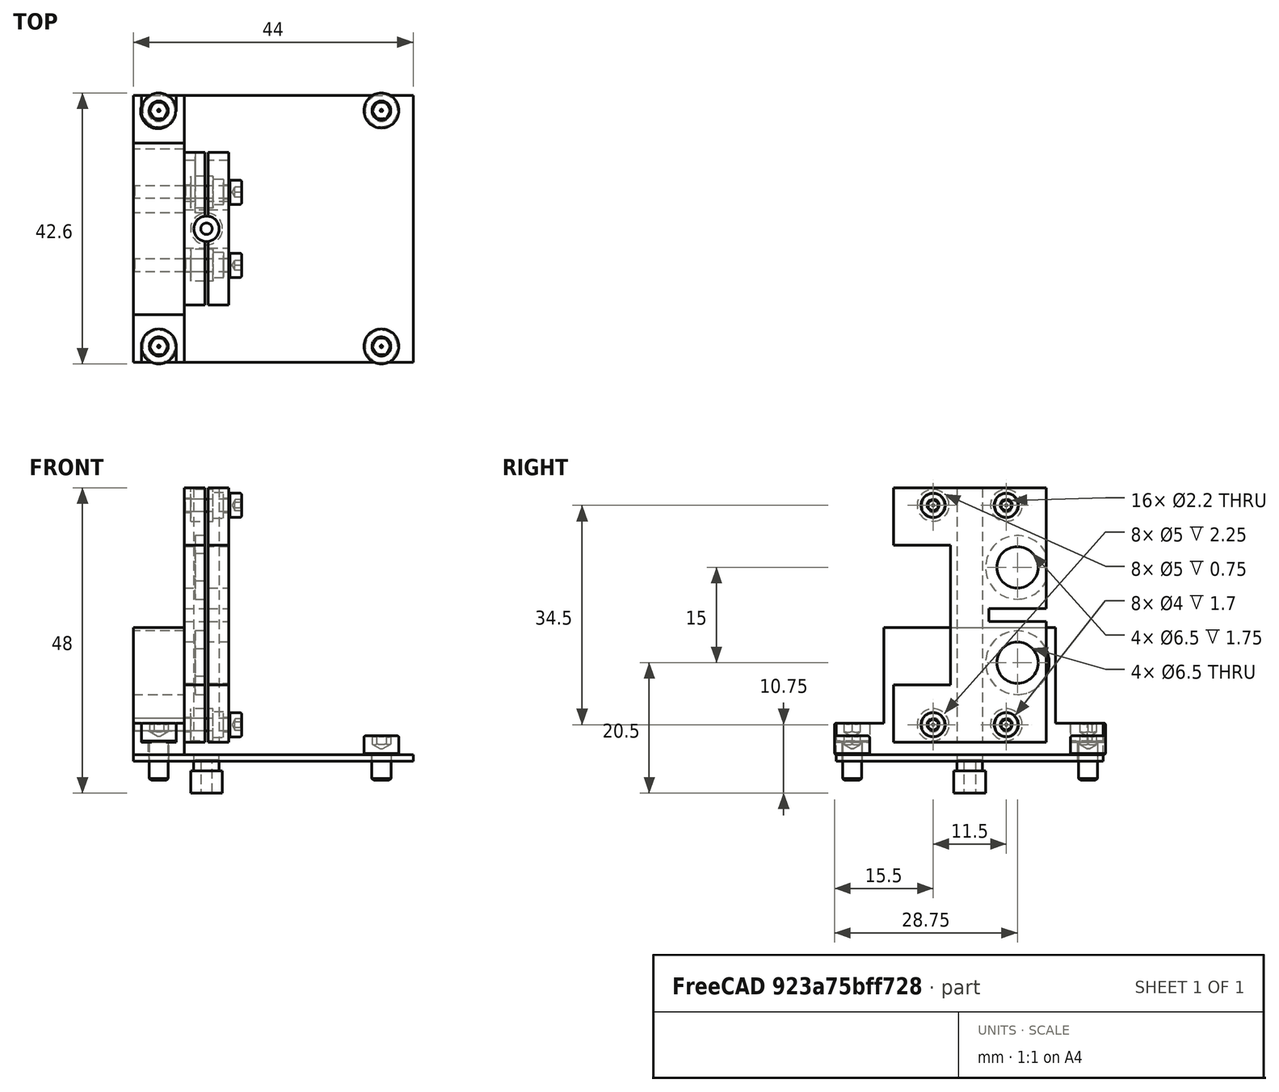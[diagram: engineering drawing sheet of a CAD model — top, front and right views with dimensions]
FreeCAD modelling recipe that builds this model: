
FCSTD DOCUMENT  (FreeCAD 0.22R0.21.2)
Label: Quak_XL30_Modulator2
License: All rights reserved
LicenseURL: http://en.wikipedia.org/wiki/All_rights_reserved
objects: TechDraw::DrawViewDimension×105, Part::Cylinder×38, Part::MultiFuse×22, App::Link×17, TechDraw::DrawProjGroupItem×12, Part::Box×11, Part::Cut×11, Part::FeaturePython×8, TechDraw::DrawSVGTemplate×8, TechDraw::DrawPage×8, Part::Feature×8, TechDraw::DrawProjGroup×4, TechDraw::DrawViewAnnotation×4, TechDraw::DrawViewPart×4, TechDraw::DrawViewSection×4, Spreadsheet::Sheet×1, Part::Compound×1
note: 264 computed .brp shape members not serialized (recipe doc carries the construction recipe); baked Part::Feature solids carry a one-line shape summary decoded from their .brp
EXTERNAL_REF file=XL30ColumnAttachmentRing_PCBKicker01.FCStd obj=Cut007
EXTERNAL_REF file=../../Spacers/Macor/4mmOD_M2_5.5mm.FCStd obj=Cut

FEATURE [Spreadsheet::Sheet] Spreadsheet  label="ModulatorParameters"
  cells = A2='Beamhole diameter; B2(beamhole_diameter)=3; G2='epsilon_r; H2(e_r)=3.5; I2='Kapton: 3.5, Vacuum 0; K2='Vacuum 'Permitivity (e0); L2='8.854187e-12; A3='Insulation spacing; B3(insulation_spacing)=0.5; G3='mu_r; H3(mu_r)=1; K3='Vacuum 'Permeability (mu0); L3='1.257e-06; A4='Maximum hole diameter; B4(max_beamhole_diameter)=6; G4='Intrinsic impedance; H4(eta_intrinsic_impedance)==sqrt(mu_r * 1.257e-06 / (e_r * 8.854187e-12)); A5='Holder minimum length; B5(holderminlength)=20; G5='Kicker imepdance; H5='=eta_intrinsic_impedance * insulation_spacing / (kicker_inner_width * kicker_plate_length); A6='Kicker length; B6(kicker_length)=40
FEATURE [App::Link] Link  label="Stackmountring02"
  LinkedObject = -> <external XL30ColumnAttachmentRing_PCBKicker01.FCStd>#Cut007
FEATURE [Part::Box] Box  label="Cube"
  AttacherType = Attacher::AttachEngine3D
  Height = 5
  Length = 8
  Placement = pos=(-11.5,-21,5) rot=(0,0,1;0rad)
  Width = 42
FEATURE [Part::FeaturePython] Screw  label="M3x6-Screw"  # Fasteners workbench fastener (typed FeaturePython)
  Placement = pos=(-7.5,18.6,8) rot=(1,0,0;0rad)
  diameter = 4
  invert = false
  leftHanded = false
  length = 10
  lengthCustom = 6
  matchOuter = false
  offset = 0
  thread = false
  type = 48
FEATURE [Part::Cylinder] Cylinder
  Angle = 360
  AttacherType = Attacher::AttachEngine3D
  FirstAngle = 0
  Height = 5
  Radius = 1.6
  SecondAngle = 0
FEATURE [Part::Cylinder] Cylinder001
  Angle = 360
  AttacherType = Attacher::AttachEngine3D
  FirstAngle = 0
  Height = 3
  Placement = pos=(0,0,2) rot=(0,0,1;0rad)
  Radius = 2.75
  SecondAngle = 0
FEATURE [Part::MultiFuse] Fusion
  Placement = pos=(-7.6,18.5,5) rot=(0,0,1;0rad)
  Shapes = -> [Cylinder001,Cylinder]
FEATURE [Part::Cylinder] Cylinder002
  Angle = 360
  AttacherType = Attacher::AttachEngine3D
  FirstAngle = 0
  Height = 5
  Radius = 1.6
  SecondAngle = 0
FEATURE [Part::Cylinder] Cylinder003
  Angle = 360
  AttacherType = Attacher::AttachEngine3D
  FirstAngle = 0
  Height = 3
  Placement = pos=(0,0,2) rot=(0,0,1;0rad)
  Radius = 2.75
  SecondAngle = 0
FEATURE [Part::MultiFuse] Fusion001
  Placement = pos=(-7.5,-18.5,5) rot=(0,0,1;0rad)
  Shapes = -> [Cylinder003,Cylinder002]
FEATURE [Part::FeaturePython] Screw001  label="M3x6-Screw001"  # Fasteners workbench fastener (typed FeaturePython)
  Placement = pos=(-7.5,-18.5,8) rot=(1,0,0;0rad)
  diameter = 4
  invert = false
  leftHanded = false
  length = 10
  lengthCustom = 6
  matchOuter = false
  offset = 0
  thread = false
  type = 48
FEATURE [Part::Box] Box001  label="Cube001"
  AttacherType = Attacher::AttachEngine3D
  Height = 3
  Length = 5.5
  Placement = pos=(-10.25,18.5,7) rot=(0,0,1;0rad)
  Width = 5.5
FEATURE [Part::Box] Box002  label="Cube002"
  AttacherType = Attacher::AttachEngine3D
  Height = 3
  Length = 5.5
  Placement = pos=(-10.25,-24,7) rot=(0,0,1;0rad)
  Width = 5.5
FEATURE [Part::MultiFuse] Fusion002
  Shapes = -> [Fusion,Box001]
FEATURE [Part::MultiFuse] Fusion003
  Shapes = -> [Fusion001,Box002]
FEATURE [Part::MultiFuse] Fusion004
  Shapes = -> [Fusion002,Fusion003]
FEATURE [Part::Cut] Cut
  Base = -> Box
  Tool = -> Fusion004
FEATURE [Part::Box] Box003  label="Cube003"
  AttacherType = Attacher::AttachEngine3D
  Height = 20
  Length = 8
  Placement = pos=(-11.5,-13.5,5) rot=(0,0,1;0rad)
  Width = 27
  expr: .Placement.Base.y = -(2 * 5.5 + <<ModulatorParameters>>.max_beamhole_diameter + 10) / 2
  expr: Height = <<ModulatorParameters>>.holderminlength
  expr: Width = 2 * 5.5 + <<ModulatorParameters>>.max_beamhole_diameter + 10
FEATURE [Part::MultiFuse] Fusion005
  Shapes = -> [Cut,Box003]
FEATURE [Part::Box] Box004  label="Cube004"
  AttacherType = Attacher::AttachEngine3D
  Height = 40
  Length = 3.25
  Placement = pos=(-3.5,-12,0) rot=(0,0,1;0rad)
  Width = 24
  expr: .Placement.Base.y = -(2 * 9 + <<ModulatorParameters>>.max_beamhole_diameter) / 2
  expr: Height = <<ModulatorParameters>>.kicker_length
  expr: Length = 3.5 - <<ModulatorParameters>>.insulation_spacing / 2
  expr: Width = 2 * 9 + <<ModulatorParameters>>.max_beamhole_diameter
FEATURE [Part::Cylinder] Cylinder004  label="Beamhole"
  Angle = 360
  AttacherType = Attacher::AttachEngine3D
  FirstAngle = 0
  Height = 40
  Radius = 2
  SecondAngle = 0
  expr: Height = <<ModulatorParameters>>.kicker_length
FEATURE [Part::Cut] Cut001
  Base = -> Box004
  Placement = pos=(0,0,7) rot=(0,0,1;0rad)
  Tool = -> Cylinder004
FEATURE [App::Link] Link001  label="Markor4mmOD_M2"
  LinkPlacement = pos=(-2.5,-5.75,9.75) rot=(0,1,0;1.5708rad)
  LinkedObject = -> <external ../../Spacers/Macor/4mmOD_M2_5.5mm.FCStd>#Cut
  Placement = pos=(-2.5,-5.75,9.75) rot=(0,1,0;1.5708rad)
  expr: .Placement.Base.y = -<<ModulatorParameters>>.max_beamhole_diameter / 2 - 5.5 / 2
FEATURE [Part::Cylinder] Cylinder006
  Angle = 360
  AttacherType = Attacher::AttachEngine3D
  FirstAngle = 0
  Height = 10
  Placement = pos=(-3.5,-5.75,9.75) rot=(0,1,0;1.5708rad)
  Radius = 1.1
  SecondAngle = 0
  expr: .Placement.Base.y = -<<ModulatorParameters>>.max_beamhole_diameter / 2 - 5.5 / 2
FEATURE [Part::Cylinder] Cylinder007
  Angle = 360
  AttacherType = Attacher::AttachEngine3D
  FirstAngle = 0
  Height = 10
  Placement = pos=(-3.5,5.75,9.75) rot=(0,1,0;1.5708rad)
  Radius = 1.1
  SecondAngle = 0
  expr: .Placement.Base.y = <<ModulatorParameters>>.max_beamhole_diameter / 2 + 5.5 / 2
FEATURE [App::Link] Link002  label="Markor4mmOD_M003"
  LinkPlacement = pos=(-2.5,5.75,9.75) rot=(0,1,0;1.5708rad)
  LinkedObject = -> <external ../../Spacers/Macor/4mmOD_M2_5.5mm.FCStd>#Cut
  Placement = pos=(-2.5,5.75,9.75) rot=(0,1,0;1.5708rad)
  expr: .Placement.Base.y = <<ModulatorParameters>>.max_beamhole_diameter / 2 + 5.5 / 2
FEATURE [Part::MultiFuse] Fusion006
  Shapes = -> [Link001,Cylinder006,Cylinder007,Link002]
FEATURE [Part::Cylinder] Cylinder008
  Angle = 360
  AttacherType = Attacher::AttachEngine3D
  FirstAngle = 0
  Height = 10
  Placement = pos=(-3.5,-5.75,44.25) rot=(0,1,0;1.5708rad)
  Radius = 1.1
  SecondAngle = 0
  expr: .Placement.Base.y = -<<ModulatorParameters>>.max_beamhole_diameter / 2 - 5.5 / 2
  expr: .Placement.Base.z = 7 + <<ModulatorParameters>>.kicker_length - 5.5 / 2
FEATURE [Part::Cylinder] Cylinder009
  Angle = 360
  AttacherType = Attacher::AttachEngine3D
  FirstAngle = 0
  Height = 10
  Placement = pos=(-3.5,5.75,44.25) rot=(0,1,0;1.5708rad)
  Radius = 1.1
  SecondAngle = 0
  expr: .Placement.Base.y = <<ModulatorParameters>>.max_beamhole_diameter / 2 + 5.5 / 2
  expr: .Placement.Base.z = 7 + <<ModulatorParameters>>.kicker_length - 5.5 / 2
FEATURE [App::Link] Link003  label="Markor4mmOD_M004"
  LinkPlacement = pos=(-2.5,-5.75,44.25) rot=(0,1,0;1.5708rad)
  LinkedObject = -> <external ../../Spacers/Macor/4mmOD_M2_5.5mm.FCStd>#Cut
  Placement = pos=(-2.5,-5.75,44.25) rot=(0,1,0;1.5708rad)
  expr: .Placement.Base.y = -1 * (<<ModulatorParameters>>.max_beamhole_diameter / 2 + 5.5 / 2)
  expr: .Placement.Base.z = 7 + <<ModulatorParameters>>.kicker_length - 5.5 / 2
FEATURE [App::Link] Link004  label="Markor4mmOD_M005"
  LinkPlacement = pos=(-2.5,5.75,44.25) rot=(0,1,0;1.5708rad)
  LinkedObject = -> <external ../../Spacers/Macor/4mmOD_M2_5.5mm.FCStd>#Cut
  Placement = pos=(-2.5,5.75,44.25) rot=(0,1,0;1.5708rad)
  expr: .Placement.Base.y = <<ModulatorParameters>>.max_beamhole_diameter / 2 + 5.5 / 2
  expr: .Placement.Base.z = 7 + <<ModulatorParameters>>.kicker_length - 5.5 / 2
FEATURE [Part::MultiFuse] Fusion007
  Shapes = -> [Cylinder008,Cylinder009,Link003,Link004]
FEATURE [Part::Box] Box006  label="Cube006"
  AttacherType = Attacher::AttachEngine3D
  Height = 2
  Length = 3.25
  Placement = pos=(-3.5,3,26) rot=(0,0,1;0rad)
  Width = 9
  expr: .Placement.Base.y = <<ModulatorParameters>>.max_beamhole_diameter / 2
  expr: .Placement.Base.z = 7 + 9 + 10
  expr: Height = <<ModulatorParameters>>.kicker_length - 2 * 9 - 20
  expr: Length = 3.5 - <<ModulatorParameters>>.insulation_spacing / 2
FEATURE [Part::Box] Box007  label="Cube007"
  AttacherType = Attacher::AttachEngine3D
  Height = 22
  Length = 3.25
  Placement = pos=(-3.5,-12,16) rot=(0,0,1;0rad)
  Width = 9
  expr: .Placement.Base.y = -<<ModulatorParameters>>.max_beamhole_diameter / 2 - 9
  expr: .Placement.Base.z = 7 + 9
  expr: Height = <<ModulatorParameters>>.kicker_length - 2 * 9
  expr: Length = 3.5 - <<ModulatorParameters>>.insulation_spacing / 2
FEATURE [Part::Cylinder] Cylinder010
  Angle = 360
  AttacherType = Attacher::AttachEngine3D
  FirstAngle = 0
  Height = 10
  Placement = pos=(-3.5,7.5,34.5) rot=(0,1,0;1.5708rad)
  Radius = 3.25
  SecondAngle = 0
  expr: .Placement.Base.y = <<ModulatorParameters>>.max_beamhole_diameter / 2 + 9 / 2
  expr: .Placement.Base.z = 7 + <<ModulatorParameters>>.kicker_length - 9 - 7 / 2
FEATURE [Part::Cylinder] Cylinder011
  Angle = 360
  AttacherType = Attacher::AttachEngine3D
  FirstAngle = 0
  Height = 10
  Placement = pos=(-3.5,7.5,19.5) rot=(0,1,0;1.5708rad)
  Radius = 3.25
  SecondAngle = 0
  expr: .Placement.Base.y = <<ModulatorParameters>>.max_beamhole_diameter / 2 + 9 / 2
  expr: .Placement.Base.z = 7 + 9 + 7 / 2
FEATURE [Part::Cylinder] Cylinder012
  Angle = 360
  AttacherType = Attacher::AttachEngine3D
  FirstAngle = 0
  Height = 10
  Placement = pos=(-12.5,7.5,19.5) rot=(0,1,0;1.5708rad)
  Radius = 5
  SecondAngle = 0
  expr: .Placement.Base.y = <<ModulatorParameters>>.max_beamhole_diameter / 2 + 9 / 2
  expr: .Placement.Base.z = 7 + 9 + 7 / 2
FEATURE [Part::MultiFuse] Fusion008
  Placement = pos=(3.75,0,0) rot=(0,0,1;0rad)
  Shapes = -> [Cylinder011,Cylinder010,Box007,Box006]
FEATURE [Part::Cut] Cut002
  Base = -> Fusion005
  Tool = -> Cylinder012
FEATURE [Part::Box] Box008  label="Cube008"
  AttacherType = Attacher::AttachEngine3D
  Height = 40
  Length = 3.25
  Placement = pos=(-3.5,-12,0) rot=(0,0,1;0rad)
  Width = 24
  expr: .Placement.Base.y = -(2 * 9 + <<ModulatorParameters>>.max_beamhole_diameter) / 2
  expr: Height = <<ModulatorParameters>>.kicker_length
  expr: Length = 3.5 - <<ModulatorParameters>>.insulation_spacing / 2
  expr: Width = 2 * 9 + <<ModulatorParameters>>.max_beamhole_diameter
FEATURE [Part::Cylinder] Cylinder013  label="Beamhole001"
  Angle = 360
  AttacherType = Attacher::AttachEngine3D
  FirstAngle = 0
  Height = 40
  Radius = 2
  SecondAngle = 0
  expr: Height = <<ModulatorParameters>>.kicker_length
FEATURE [Part::Cut] Cut003
  Base = -> Box008
  Placement = pos=(0,0,7) rot=(0,0,1;3.14159rad)
  Tool = -> Cylinder013
FEATURE [Part::Box] Box009  label="Cube009"
  AttacherType = Attacher::AttachEngine3D
  Height = 2
  Length = 3.25
  Placement = pos=(-3.5,3,26) rot=(0,0,1;0rad)
  Width = 9
  expr: .Placement.Base.y = <<ModulatorParameters>>.max_beamhole_diameter / 2
  expr: .Placement.Base.z = 7 + 9 + 10
  expr: Height = <<ModulatorParameters>>.kicker_length - 2 * 9 - 20
  expr: Length = 3.5 - <<ModulatorParameters>>.insulation_spacing / 2
FEATURE [Part::Box] Box010  label="Cube010"
  AttacherType = Attacher::AttachEngine3D
  Height = 22
  Length = 3.25
  Placement = pos=(-3.5,-12,16) rot=(0,0,1;0rad)
  Width = 9
  expr: .Placement.Base.y = -<<ModulatorParameters>>.max_beamhole_diameter / 2 - 9
  expr: .Placement.Base.z = 7 + 9
  expr: Height = <<ModulatorParameters>>.kicker_length - 2 * 9
  expr: Length = 3.5 - <<ModulatorParameters>>.insulation_spacing / 2
FEATURE [Part::Cylinder] Cylinder014
  Angle = 360
  AttacherType = Attacher::AttachEngine3D
  FirstAngle = 0
  Height = 10
  Placement = pos=(-3.5,-5.75,9.75) rot=(0,1,0;1.5708rad)
  Radius = 1.1
  SecondAngle = 0
  expr: .Placement.Base.y = -<<ModulatorParameters>>.max_beamhole_diameter / 2 - 5.5 / 2
FEATURE [Part::Cylinder] Cylinder015
  Angle = 360
  AttacherType = Attacher::AttachEngine3D
  FirstAngle = 0
  Height = 10
  Placement = pos=(-3.5,5.75,9.75) rot=(0,1,0;1.5708rad)
  Radius = 1.1
  SecondAngle = 0
  expr: .Placement.Base.y = <<ModulatorParameters>>.max_beamhole_diameter / 2 + 5.5 / 2
FEATURE [Part::Cylinder] Cylinder016
  Angle = 360
  AttacherType = Attacher::AttachEngine3D
  FirstAngle = 0
  Height = 10
  Placement = pos=(-3.5,-5.75,44.25) rot=(0,1,0;1.5708rad)
  Radius = 1.1
  SecondAngle = 0
  expr: .Placement.Base.y = -<<ModulatorParameters>>.max_beamhole_diameter / 2 - 5.5 / 2
  expr: .Placement.Base.z = 7 + <<ModulatorParameters>>.kicker_length - 5.5 / 2
FEATURE [Part::Cylinder] Cylinder017
  Angle = 360
  AttacherType = Attacher::AttachEngine3D
  FirstAngle = 0
  Height = 10
  Placement = pos=(-3.5,5.75,44.25) rot=(0,1,0;1.5708rad)
  Radius = 1.1
  SecondAngle = 0
  expr: .Placement.Base.y = <<ModulatorParameters>>.max_beamhole_diameter / 2 + 5.5 / 2
  expr: .Placement.Base.z = 7 + <<ModulatorParameters>>.kicker_length - 5.5 / 2
FEATURE [Part::Cylinder] Cylinder018
  Angle = 360
  AttacherType = Attacher::AttachEngine3D
  FirstAngle = 0
  Height = 10
  Placement = pos=(-3.5,7.5,34.5) rot=(0,1,0;1.5708rad)
  Radius = 3.25
  SecondAngle = 0
  expr: .Placement.Base.y = <<ModulatorParameters>>.max_beamhole_diameter / 2 + 9 / 2
  expr: .Placement.Base.z = 7 + <<ModulatorParameters>>.kicker_length - 9 - 7 / 2
FEATURE [Part::Cylinder] Cylinder019
  Angle = 360
  AttacherType = Attacher::AttachEngine3D
  FirstAngle = 0
  Height = 10
  Placement = pos=(-3.5,7.5,19.5) rot=(0,1,0;1.5708rad)
  Radius = 3.25
  SecondAngle = 0
  expr: .Placement.Base.y = <<ModulatorParameters>>.max_beamhole_diameter / 2 + 9 / 2
  expr: .Placement.Base.z = 7 + 9 + 7 / 2
FEATURE [App::Link] Link005  label="Markor4mmOD_M006"
  LinkPlacement = pos=(-2.5,-5.75,9.75) rot=(0,1,0;1.5708rad)
  LinkedObject = -> Cut004
  Placement = pos=(-2.5,-5.75,9.75) rot=(0,1,0;1.5708rad)
  expr: .Placement.Base.y = -<<ModulatorParameters>>.max_beamhole_diameter / 2 - 5.5 / 2
FEATURE [App::Link] Link006  label="Markor4mmOD_M007"
  LinkPlacement = pos=(-2.5,5.75,9.75) rot=(0,1,0;1.5708rad)
  LinkedObject = -> Cut004
  Placement = pos=(-2.5,5.75,9.75) rot=(0,1,0;1.5708rad)
  expr: .Placement.Base.y = <<ModulatorParameters>>.max_beamhole_diameter / 2 + 5.5 / 2
FEATURE [Part::MultiFuse] Fusion009
  Shapes = -> [Link005,Cylinder014,Cylinder015,Link006]
FEATURE [App::Link] Link007  label="Markor4mmOD_M008"
  LinkPlacement = pos=(-2.5,-5.75,44.25) rot=(0,1,0;1.5708rad)
  LinkedObject = -> Cut004
  Placement = pos=(-2.5,-5.75,44.25) rot=(0,1,0;1.5708rad)
  expr: .Placement.Base.y = -1 * (<<ModulatorParameters>>.max_beamhole_diameter / 2 + 5.5 / 2)
  expr: .Placement.Base.z = 7 + <<ModulatorParameters>>.kicker_length - 5.5 / 2
FEATURE [App::Link] Link008  label="Markor4mmOD_M009"
  LinkPlacement = pos=(-2.5,5.75,44.25) rot=(0,1,0;1.5708rad)
  LinkedObject = -> Cut004
  Placement = pos=(-2.5,5.75,44.25) rot=(0,1,0;1.5708rad)
  expr: .Placement.Base.y = <<ModulatorParameters>>.max_beamhole_diameter / 2 + 5.5 / 2
  expr: .Placement.Base.z = 7 + <<ModulatorParameters>>.kicker_length - 5.5 / 2
FEATURE [Part::MultiFuse] Fusion010
  Shapes = -> [Cylinder016,Cylinder017,Link007,Link008]
FEATURE [Part::Cylinder] Cylinder020
  Angle = 360
  AttacherType = Attacher::AttachEngine3D
  FirstAngle = 0
  Height = 3.5
  Radius = 2.5
  SecondAngle = 0
FEATURE [Part::Cylinder] Cylinder021
  Angle = 360
  AttacherType = Attacher::AttachEngine3D
  FirstAngle = 0
  Height = 5.2
  Radius = 2
  SecondAngle = 0
FEATURE [Part::Cylinder] Cylinder022
  Angle = 360
  AttacherType = Attacher::AttachEngine3D
  FirstAngle = 0
  Height = 10
  Radius = 0.9
  SecondAngle = 0
FEATURE [Part::MultiFuse] Fusion012
  Shapes = -> [Cylinder021,Cylinder020]
FEATURE [Part::Cut] Cut004  label="Markor4mmOD_M010"
  Base = -> Fusion012
  Tool = -> Cylinder022
FEATURE [Part::MultiFuse] Fusion013
  Shapes = -> [Fusion006,Fusion007,Fusion008]
FEATURE [Part::MultiFuse] Fusion014
  Shapes = -> [Fusion013,Fusion010,Fusion009]
FEATURE [Part::Cut] Cut006  label="CopperB"
  Base = -> Cut003
  Placement = pos=(0,0,1) rot=(0,0,1;0rad)
  Tool = -> Fusion014
FEATURE [Part::Cylinder] Cylinder023
  Angle = 360
  AttacherType = Attacher::AttachEngine3D
  FirstAngle = 0
  Height = 1.5
  Placement = pos=(-1.75,7.5,34.5) rot=(0,1,0;1.5708rad)
  Radius = 5
  SecondAngle = 0
  expr: .Placement.Base.x = -1.5 - <<ModulatorParameters>>.insulation_spacing / 2
  expr: .Placement.Base.y = <<ModulatorParameters>>.max_beamhole_diameter / 2 + 9 / 2
  expr: .Placement.Base.z = 7 + <<ModulatorParameters>>.kicker_length - 9 - 7 / 2
FEATURE [Part::Cylinder] Cylinder024
  Angle = 360
  AttacherType = Attacher::AttachEngine3D
  FirstAngle = 0
  Height = 1.5
  Placement = pos=(-1.75,7.5,19.5) rot=(0,1,0;1.5708rad)
  Radius = 5
  SecondAngle = 0
  expr: .Placement.Base.x = -1.5 - <<ModulatorParameters>>.insulation_spacing / 2
  expr: .Placement.Base.y = <<ModulatorParameters>>.max_beamhole_diameter / 2 + 9 / 2
  expr: .Placement.Base.z = 7 + 9 + 7 / 2
FEATURE [Part::MultiFuse] Fusion015
  Shapes = -> [Cylinder023,Cylinder024]
FEATURE [Part::MultiFuse] Fusion011
  Shapes = -> [Cylinder019,Cylinder018,Box010,Box009,Fusion015]
FEATURE [Part::Cut] Cut005
  Base = -> Cut001
  Tool = -> Fusion011
FEATURE [Part::Cylinder] Cylinder025
  Angle = 360
  AttacherType = Attacher::AttachEngine3D
  FirstAngle = 0
  Height = 10
  Placement = pos=(-3.5,-5.75,9.75) rot=(0,1,0;1.5708rad)
  Radius = 1.1
  SecondAngle = 0
  expr: .Placement.Base.y = -<<ModulatorParameters>>.max_beamhole_diameter / 2 - 5.5 / 2
FEATURE [Part::Cylinder] Cylinder026
  Angle = 360
  AttacherType = Attacher::AttachEngine3D
  FirstAngle = 0
  Height = 10
  Placement = pos=(-3.5,5.75,9.75) rot=(0,1,0;1.5708rad)
  Radius = 1.1
  SecondAngle = 0
  expr: .Placement.Base.y = <<ModulatorParameters>>.max_beamhole_diameter / 2 + 5.5 / 2
FEATURE [Part::Cylinder] Cylinder027
  Angle = 360
  AttacherType = Attacher::AttachEngine3D
  FirstAngle = 0
  Height = 10
  Placement = pos=(-3.5,-5.75,44.25) rot=(0,1,0;1.5708rad)
  Radius = 1.1
  SecondAngle = 0
  expr: .Placement.Base.y = -<<ModulatorParameters>>.max_beamhole_diameter / 2 - 5.5 / 2
  expr: .Placement.Base.z = 7 + <<ModulatorParameters>>.kicker_length - 5.5 / 2
FEATURE [Part::Cylinder] Cylinder028
  Angle = 360
  AttacherType = Attacher::AttachEngine3D
  FirstAngle = 0
  Height = 10
  Placement = pos=(-3.5,5.75,44.25) rot=(0,1,0;1.5708rad)
  Radius = 1.1
  SecondAngle = 0
  expr: .Placement.Base.y = <<ModulatorParameters>>.max_beamhole_diameter / 2 + 5.5 / 2
  expr: .Placement.Base.z = 7 + <<ModulatorParameters>>.kicker_length - 5.5 / 2
FEATURE [Part::Cylinder] Cylinder029
  Angle = 360
  AttacherType = Attacher::AttachEngine3D
  FirstAngle = 0
  Height = 3.5
  Radius = 2.5
  SecondAngle = 0
FEATURE [Part::Cylinder] Cylinder030
  Angle = 360
  AttacherType = Attacher::AttachEngine3D
  FirstAngle = 0
  Height = 5.2
  Radius = 2
  SecondAngle = 0
FEATURE [Part::Cylinder] Cylinder031
  Angle = 360
  AttacherType = Attacher::AttachEngine3D
  FirstAngle = 0
  Height = 10
  Radius = 0.9
  SecondAngle = 0
FEATURE [Part::MultiFuse] Fusion018
  Shapes = -> [Cylinder030,Cylinder029]
FEATURE [Part::Cut] Cut007  label="Markor4mmOD_M011"
  Base = -> Fusion018
  Tool = -> Cylinder031
FEATURE [App::Link] Link009  label="Markor4mmOD_M012"
  LinkPlacement = pos=(-2.5,-5.75,9.75) rot=(0,1,0;1.5708rad)
  LinkedObject = -> Cut007
  Placement = pos=(-2.5,-5.75,9.75) rot=(0,1,0;1.5708rad)
  expr: .Placement.Base.y = -<<ModulatorParameters>>.max_beamhole_diameter / 2 - 5.5 / 2
FEATURE [App::Link] Link010  label="Markor4mmOD_M013"
  LinkPlacement = pos=(-2.5,5.75,9.75) rot=(0,1,0;1.5708rad)
  LinkedObject = -> Cut007
  Placement = pos=(-2.5,5.75,9.75) rot=(0,1,0;1.5708rad)
  expr: .Placement.Base.y = <<ModulatorParameters>>.max_beamhole_diameter / 2 + 5.5 / 2
FEATURE [Part::MultiFuse] Fusion016
  Shapes = -> [Link009,Cylinder025,Cylinder026,Link010]
FEATURE [App::Link] Link011  label="Markor4mmOD_M014"
  LinkPlacement = pos=(-2.5,-5.75,44.25) rot=(0,1,0;1.5708rad)
  LinkedObject = -> Cut007
  Placement = pos=(-2.5,-5.75,44.25) rot=(0,1,0;1.5708rad)
  expr: .Placement.Base.y = -1 * (<<ModulatorParameters>>.max_beamhole_diameter / 2 + 5.5 / 2)
  expr: .Placement.Base.z = 7 + <<ModulatorParameters>>.kicker_length - 5.5 / 2
FEATURE [App::Link] Link012  label="Markor4mmOD_M015"
  LinkPlacement = pos=(-2.5,5.75,44.25) rot=(0,1,0;1.5708rad)
  LinkedObject = -> Cut007
  Placement = pos=(-2.5,5.75,44.25) rot=(0,1,0;1.5708rad)
  expr: .Placement.Base.y = <<ModulatorParameters>>.max_beamhole_diameter / 2 + 5.5 / 2
  expr: .Placement.Base.z = 7 + <<ModulatorParameters>>.kicker_length - 5.5 / 2
FEATURE [Part::MultiFuse] Fusion017
  Shapes = -> [Cylinder027,Cylinder028,Link011,Link012]
FEATURE [Part::MultiFuse] Fusion019
  Shapes = -> [Fusion016,Fusion017]
FEATURE [Part::Cut] Cut008  label="CopperA"
  Base = -> Cut005
  Placement = pos=(0,0,1) rot=(0,0,1;0rad)
  Tool = -> Fusion019
FEATURE [Part::Cylinder] Cylinder032
  Angle = 360
  AttacherType = Attacher::AttachEngine3D
  FirstAngle = 0
  Height = 20
  Placement = pos=(-15,-5.75,9.75) rot=(0,1,0;1.5708rad)
  Radius = 1
  SecondAngle = 0
  expr: .Placement.Base.y = -<<ModulatorParameters>>.max_beamhole_diameter / 2 - 5.5 / 2
FEATURE [Part::Cylinder] Cylinder033
  Angle = 360
  AttacherType = Attacher::AttachEngine3D
  FirstAngle = 0
  Height = 20
  Placement = pos=(-15,5.75,9.75) rot=(0,1,0;1.5708rad)
  Radius = 1
  SecondAngle = 0
  expr: .Placement.Base.y = <<ModulatorParameters>>.max_beamhole_diameter / 2 + 5.5 / 2
FEATURE [Part::MultiFuse] Fusion020
  Shapes = -> [Cylinder032,Cylinder033]
FEATURE [Part::Cut] Cut009  label="Holder"
  Base = -> Cut002
  Placement = pos=(0,0,1) rot=(0,0,1;0rad)
  Tool = -> Fusion020
FEATURE [Part::FeaturePython] Screw002  label="M2x15-Screw"  # Fasteners workbench fastener (typed FeaturePython)
  Placement = pos=(3.5,5.75,10.75) rot=(0,1,0;1.5708rad)
  diameter = 2
  invert = false
  leftHanded = false
  length = 10
  lengthCustom = 15
  matchOuter = false
  offset = 0
  thread = false
  type = 48
  expr: .Placement.Base.y = <<ModulatorParameters>>.max_beamhole_diameter / 2 + 5.5 / 2
FEATURE [Part::FeaturePython] Screw003  label="M2x15-Screw001"  # Fasteners workbench fastener (typed FeaturePython)
  Placement = pos=(3.5,-5.75,10.75) rot=(0,1,0;1.5708rad)
  diameter = 2
  invert = false
  leftHanded = false
  length = 10
  lengthCustom = 15
  matchOuter = false
  offset = 0
  thread = false
  type = 48
  expr: .Placement.Base.y = -1 * (<<ModulatorParameters>>.max_beamhole_diameter / 2 + 5.5 / 2)
FEATURE [Part::FeaturePython] Screw004  label="M2x7-Screw"  # Fasteners workbench fastener (typed FeaturePython)
  Placement = pos=(3.5,5.75,45.25) rot=(0,1,0;1.5708rad)
  diameter = 2
  invert = false
  leftHanded = false
  length = 10
  lengthCustom = 7
  matchOuter = false
  offset = 0
  thread = false
  type = 48
  expr: .Placement.Base.y = <<ModulatorParameters>>.max_beamhole_diameter / 2 + 5.5 / 2
  expr: .Placement.Base.z = 7 + <<ModulatorParameters>>.kicker_length - 5.5 / 2 + 1
FEATURE [Part::FeaturePython] Screw005  label="M2x7-Screw001"  # Fasteners workbench fastener (typed FeaturePython)
  Placement = pos=(3.5,-5.75,45.25) rot=(0,1,0;1.5708rad)
  diameter = 2
  invert = false
  leftHanded = false
  length = 10
  lengthCustom = 7
  matchOuter = false
  offset = 0
  thread = false
  type = 48
  expr: .Placement.Base.y = -1 * (<<ModulatorParameters>>.max_beamhole_diameter / 2 + 5.5 / 2)
  expr: .Placement.Base.z = 7 + <<ModulatorParameters>>.kicker_length - 5.5 / 2 + 1
FEATURE [App::Link] Link013  label="Markor4mmOD_M016"
  LinkPlacement = pos=(-2.5,-5.75,45.25) rot=(0,1,0;1.5708rad)
  LinkedObject = -> <external ../../Spacers/Macor/4mmOD_M2_5.5mm.FCStd>#Cut
  Placement = pos=(-2.5,-5.75,45.25) rot=(0,1,0;1.5708rad)
  expr: .Placement.Base.y = -1 * (<<ModulatorParameters>>.max_beamhole_diameter / 2 + 5.5 / 2)
  expr: .Placement.Base.z = 7 + <<ModulatorParameters>>.kicker_length - 5.5 / 2 + 1
FEATURE [App::Link] Link014  label="Markor4mmOD_M017"
  LinkPlacement = pos=(-2.5,-5.75,10.75) rot=(0,1,0;1.5708rad)
  LinkedObject = -> <external ../../Spacers/Macor/4mmOD_M2_5.5mm.FCStd>#Cut
  Placement = pos=(-2.5,-5.75,10.75) rot=(0,1,0;1.5708rad)
  expr: .Placement.Base.y = -1 * (<<ModulatorParameters>>.max_beamhole_diameter / 2 + 5.5 / 2)
FEATURE [App::Link] Link015  label="Markor4mmOD_M018"
  LinkPlacement = pos=(-2.5,5.75,45.25) rot=(0,1,0;1.5708rad)
  LinkedObject = -> <external ../../Spacers/Macor/4mmOD_M2_5.5mm.FCStd>#Cut
  Placement = pos=(-2.5,5.75,45.25) rot=(0,1,0;1.5708rad)
  expr: .Placement.Base.y = <<ModulatorParameters>>.max_beamhole_diameter / 2 + 5.5 / 2
  expr: .Placement.Base.z = 7 + <<ModulatorParameters>>.kicker_length - 5.5 / 2 + 1
FEATURE [App::Link] Link016  label="Markor4mmOD_M019"
  LinkPlacement = pos=(-2.5,5.75,10.75) rot=(0,1,0;1.5708rad)
  LinkedObject = -> <external ../../Spacers/Macor/4mmOD_M2_5.5mm.FCStd>#Cut
  Placement = pos=(-2.5,5.75,10.75) rot=(0,1,0;1.5708rad)
  expr: .Placement.Base.y = <<ModulatorParameters>>.max_beamhole_diameter / 2 + 5.5 / 2
FEATURE [Part::Box] Box011  label="Cube011"
  AttacherType = Attacher::AttachEngine3D
  Height = 1
  Length = 44
  Placement = pos=(-11.5,-21,1) rot=(0,0,1;0rad)
  Width = 42
  expr: .Placement.Base.x = -10.25 + 5.5 / 2 - 4
  expr: .Placement.Base.y = -21
FEATURE [Part::Cylinder] Cylinder034
  Angle = 360
  AttacherType = Attacher::AttachEngine3D
  FirstAngle = 0
  Height = 10
  Placement = pos=(-7.5,-18.5,0) rot=(0,0,1;0rad)
  Radius = 1.6
  SecondAngle = 0
FEATURE [Part::Cylinder] Cylinder035
  Angle = 360
  AttacherType = Attacher::AttachEngine3D
  FirstAngle = 0
  Height = 10
  Placement = pos=(-7.5,18.5,0) rot=(0,0,1;0rad)
  Radius = 1.6
  SecondAngle = 0
FEATURE [Part::Cylinder] Cylinder036
  Angle = 360
  AttacherType = Attacher::AttachEngine3D
  FirstAngle = 0
  Height = 10
  Placement = pos=(27.5,-18.5,0) rot=(0,0,1;0rad)
  Radius = 1.6
  SecondAngle = 0
FEATURE [Part::Cylinder] Cylinder037
  Angle = 360
  AttacherType = Attacher::AttachEngine3D
  FirstAngle = 0
  Height = 10
  Placement = pos=(27.5,18.5,0) rot=(0,0,1;0rad)
  Radius = 1.6
  SecondAngle = 0
FEATURE [Part::Cylinder] Cylinder038
  Angle = 360
  AttacherType = Attacher::AttachEngine3D
  FirstAngle = 0
  Height = 10
  Radius = 2
  SecondAngle = 0
FEATURE [Part::MultiFuse] Fusion021
  Shapes = -> [Cylinder038,Cylinder034,Cylinder035,Cylinder036,Cylinder037]
FEATURE [Part::Cut] Cut010  label="CopperPlate"
  Base = -> Box011
  Placement = pos=(0,0,4) rot=(0,0,1;0rad)
  Tool = -> Fusion021
FEATURE [Part::FeaturePython] Screw006  label="M3x4-Screw"  # Fasteners workbench fastener (typed FeaturePython)
  Placement = pos=(27.5,18.6,6) rot=(1,0,0;0rad)
  diameter = 4
  invert = false
  leftHanded = false
  length = 10
  lengthCustom = 4
  matchOuter = false
  offset = 0
  thread = false
  type = 48
FEATURE [Part::FeaturePython] Screw007  label="M3x4-Screw001"  # Fasteners workbench fastener (typed FeaturePython)
  Placement = pos=(27.5,-18.5,6) rot=(1,0,0;0rad)
  diameter = 4
  invert = false
  leftHanded = false
  length = 10
  lengthCustom = 4
  matchOuter = false
  offset = 0
  thread = false
  type = 48
FEATURE [TechDraw::DrawSVGTemplate] Template
  EditableTexts = Designed_by_Name=Thomas Spielauer; FC-Date=2024-05-15; FC-SC=mm; FC-SH=1/1; FC-Title=Unshielded Kicker, 40mm; Subtitle=XL30 Column Mount, Mount
  Height = 210
  Orientation = 1
  Template = <path>
  Width = 297
FEATURE [TechDraw::DrawProjGroupItem] ProjItem  label="Front"
  CoarseView = false
  Direction = (1,0,0)
  Focus = 100
  HardHidden = false
  IsoCount = 0
  IsoHidden = false
  IsoVisible = false
  LockPosition = true
  Perspective = false
  Rotation = 0
  RotationVector = (0,1,0)
  Scale = 2
  ScaleType = 2
  ScrubCount = 0
  SeamHidden = false
  SeamVisible = false
  SmoothHidden = false
  SmoothVisible = true
  Source = -> [Cut009]
  Type = 0
  X = 0
  XDirection = (0,1,0)
  Y = 0
FEATURE [TechDraw::DrawProjGroupItem] ProjItem001  label="Left"
  CoarseView = false
  Direction = (1e-16,-1,0)
  Focus = 100
  HardHidden = false
  IsoCount = 0
  IsoHidden = false
  IsoVisible = false
  LockPosition = false
  Perspective = false
  Rotation = 0
  RotationVector = (1,0,0)
  ScaleType = 2
  ScrubCount = 0
  SeamHidden = false
  SeamVisible = false
  SmoothHidden = false
  SmoothVisible = true
  Source = -> [Cut009]
  Type = 1
  X = 94.5278
  XDirection = (1,1e-16,0)
  Y = 0
FEATURE [TechDraw::DrawProjGroupItem] ProjItem002  label="Top"
  CoarseView = false
  Direction = (0,0,1)
  Focus = 100
  HardHidden = false
  IsoCount = 0
  IsoHidden = false
  IsoVisible = false
  LockPosition = false
  Perspective = false
  Rotation = 0
  RotationVector = (1,0,0)
  ScaleType = 2
  ScrubCount = 0
  SeamHidden = false
  SeamVisible = false
  SmoothHidden = false
  SmoothVisible = true
  Source = -> [Cut009]
  Type = 4
  X = 0
  XDirection = (0,1,0)
  Y = -89.2298
FEATURE [TechDraw::DrawProjGroupItem] ProjItem003  label="FrontTopRight"
  CoarseView = false
  Direction = (0.57735,0.57735,0.57735)
  Focus = 100
  HardHidden = false
  IsoCount = 0
  IsoHidden = false
  IsoVisible = false
  LockPosition = false
  Perspective = false
  Rotation = 0
  RotationVector = (1,0,0)
  ScaleType = 2
  ScrubCount = 0
  SeamHidden = false
  SeamVisible = false
  SmoothHidden = false
  SmoothVisible = true
  Source = -> [Cut009]
  Type = 7
  X = 166.748
  XDirection = (-0.707107,0.707107,0)
  Y = -18.1703
FEATURE [TechDraw::DrawProjGroup] ProjGroup
  Anchor = -> ProjItem
  AutoDistribute = false
  LockPosition = false
  ProjectionType = 0
  Rotation = 0
  Scale = 2
  ScaleType = 2
  Source = -> [Cut009]
  Views = -> [ProjItem,ProjItem001,ProjItem002,ProjItem003]
  X = 69.6549
  Y = 162.841
  spacingX = 15
  spacingY = 15
FEATURE [TechDraw::DrawViewDimension] Dimension
  AngleOverride = false
  Arbitrary = false
  ArbitraryTolerances = false
  EqualTolerance = true
  ExtensionAngle = 0
  FormatSpec = %.2w
  FormatSpecOverTolerance = %+.2w
  FormatSpecUnderTolerance = %+.2w
  Inverted = false
  LineAngle = 0
  LockPosition = false
  MeasureType = 1
  OverTolerance = 0
  References2D = -> [ProjItem]
  Rotation = 0
  ScaleType = 0
  TheoreticalExact = false
  Type = 1
  UnderTolerance = 0
  X = 50.3463
  Y = -24.1585
FEATURE [TechDraw::DrawViewDimension] Dimension001
  AngleOverride = false
  Arbitrary = false
  ArbitraryTolerances = false
  EqualTolerance = true
  ExtensionAngle = 0
  FormatSpec = ⌀%.2w (M3 through)
  FormatSpecOverTolerance = %+.2w
  FormatSpecUnderTolerance = %+.2w
  Inverted = false
  LineAngle = 0
  LockPosition = false
  MeasureType = 1
  OverTolerance = 0
  References2D = -> [ProjItem002]
  Rotation = 0
  ScaleType = 0
  TheoreticalExact = false
  Type = 5
  UnderTolerance = 0
  X = 78.1076
  Y = 23.0344
FEATURE [TechDraw::DrawViewDimension] Dimension002
  AngleOverride = false
  Arbitrary = false
  ArbitraryTolerances = false
  EqualTolerance = true
  ExtensionAngle = 0
  FormatSpec = ⌀%.2w
  FormatSpecOverTolerance = %+.2w
  FormatSpecUnderTolerance = %+.2w
  Inverted = false
  LineAngle = 0
  LockPosition = false
  MeasureType = 1
  OverTolerance = 0
  References2D = -> [ProjItem002]
  Rotation = 0
  ScaleType = 0
  TheoreticalExact = false
  Type = 5
  UnderTolerance = 0
  X = 60.5132
  Y = -1.32495
FEATURE [TechDraw::DrawViewDimension] Dimension003
  AngleOverride = false
  Arbitrary = false
  ArbitraryTolerances = false
  EqualTolerance = true
  ExtensionAngle = 0
  FormatSpec = %.2w
  FormatSpecOverTolerance = %+.2w
  FormatSpecUnderTolerance = %+.2w
  Inverted = false
  LineAngle = 0
  LockPosition = false
  MeasureType = 1
  OverTolerance = 0
  References2D = -> [ProjItem002]
  Rotation = 0
  ScaleType = 0
  TheoreticalExact = false
  Type = 2
  UnderTolerance = 0
  X = 76.3588
  Y = 13.4001
FEATURE [TechDraw::DrawViewDimension] Dimension004
  AngleOverride = false
  Arbitrary = false
  ArbitraryTolerances = false
  EqualTolerance = true
  ExtensionAngle = 0
  FormatSpec = %.2w
  FormatSpecOverTolerance = %+.2w
  FormatSpecUnderTolerance = %+.2w
  Inverted = false
  LineAngle = 0
  LockPosition = false
  MeasureType = 1
  OverTolerance = 0
  References2D = -> [ProjItem001]
  Rotation = 0
  ScaleType = 0
  TheoreticalExact = false
  Type = 1
  UnderTolerance = 0
  X = 14.6019
  Y = -21.1642
FEATURE [TechDraw::DrawViewDimension] Dimension005
  AngleOverride = false
  Arbitrary = false
  ArbitraryTolerances = false
  EqualTolerance = true
  ExtensionAngle = 0
  FormatSpec = %.2w
  FormatSpecOverTolerance = %+.2w
  FormatSpecUnderTolerance = %+.2w
  Inverted = false
  LineAngle = 0
  LockPosition = false
  MeasureType = 1
  OverTolerance = 0
  References2D = -> [ProjItem]
  Rotation = 0
  ScaleType = 0
  TheoreticalExact = false
  Type = 2
  UnderTolerance = 0
  X = 52.937
  Y = -3.00298
FEATURE [TechDraw::DrawViewDimension] Dimension006
  AngleOverride = false
  Arbitrary = false
  ArbitraryTolerances = false
  EqualTolerance = true
  ExtensionAngle = 0
  FormatSpec = %.2w
  FormatSpecOverTolerance = %+.2w
  FormatSpecUnderTolerance = %+.2w
  Inverted = false
  LineAngle = 0
  LockPosition = false
  MeasureType = 1
  OverTolerance = 0
  References2D = -> [ProjItem]
  Rotation = 0
  ScaleType = 0
  TheoreticalExact = false
  Type = 1
  UnderTolerance = 0
  X = 55.0635
  Y = 11.0611
FEATURE [TechDraw::DrawViewDimension] Dimension007
  AngleOverride = false
  Arbitrary = false
  ArbitraryTolerances = false
  EqualTolerance = true
  ExtensionAngle = 0
  FormatSpec = %.2w
  FormatSpecOverTolerance = %+.2w
  FormatSpecUnderTolerance = %+.2w
  Inverted = false
  LineAngle = 0
  LockPosition = false
  MeasureType = 1
  OverTolerance = 0
  References2D = -> [ProjItem]
  Rotation = 0
  ScaleType = 0
  TheoreticalExact = false
  Type = 1
  UnderTolerance = 0
  X = -51.3623
  Y = 8.49225
FEATURE [TechDraw::DrawViewDimension] Dimension008
  AngleOverride = false
  Arbitrary = false
  ArbitraryTolerances = false
  EqualTolerance = true
  ExtensionAngle = 0
  FormatSpec = %.2w
  FormatSpecOverTolerance = %+.2w
  FormatSpecUnderTolerance = %+.2w
  Inverted = false
  LineAngle = 0
  LockPosition = false
  MeasureType = 1
  OverTolerance = 0
  References2D = -> [ProjItem]
  Rotation = 0
  ScaleType = 0
  TheoreticalExact = false
  Type = 2
  UnderTolerance = 0
  X = -50.2917
  Y = -3.039
FEATURE [TechDraw::DrawViewDimension] Dimension009
  AngleOverride = false
  Arbitrary = false
  ArbitraryTolerances = false
  EqualTolerance = true
  ExtensionAngle = 0
  FormatSpec = ⌀%.2w (M2 thread)
  FormatSpecOverTolerance = %+.2w
  FormatSpecUnderTolerance = %+.2w
  Inverted = false
  LineAngle = 0
  LockPosition = false
  MeasureType = 1
  OverTolerance = 0
  References2D = -> [ProjItem]
  Rotation = 0
  ScaleType = 0
  TheoreticalExact = false
  Type = 5
  UnderTolerance = 0
  X = -6.28379
  Y = -42.8374
FEATURE [TechDraw::DrawViewDimension] Dimension010
  AngleOverride = false
  Arbitrary = false
  ArbitraryTolerances = false
  EqualTolerance = true
  ExtensionAngle = 0
  FormatSpec = ⌀%.2w (M2 thread)
  FormatSpecOverTolerance = %+.2w
  FormatSpecUnderTolerance = %+.2w
  Inverted = false
  LineAngle = 0
  LockPosition = false
  MeasureType = 1
  OverTolerance = 0
  References2D = -> [ProjItem]
  Rotation = 0
  ScaleType = 0
  TheoreticalExact = false
  Type = 5
  UnderTolerance = 0
  X = 16.8858
  Y = -42.325
FEATURE [TechDraw::DrawViewDimension] Dimension011
  AngleOverride = false
  Arbitrary = false
  ArbitraryTolerances = false
  EqualTolerance = true
  ExtensionAngle = 0
  FormatSpec = ⌀%.2w
  FormatSpecOverTolerance = %+.2w
  FormatSpecUnderTolerance = %+.2w
  Inverted = false
  LineAngle = 0
  LockPosition = false
  MeasureType = 1
  OverTolerance = 0
  References2D = -> [ProjItem]
  Rotation = 0
  ScaleType = 0
  TheoreticalExact = false
  Type = 5
  UnderTolerance = 0
  X = 53.3082
  Y = 32.6255
FEATURE [TechDraw::DrawViewDimension] Dimension012
  AngleOverride = false
  Arbitrary = false
  ArbitraryTolerances = false
  EqualTolerance = true
  ExtensionAngle = 0
  FormatSpec = %.2w
  FormatSpecOverTolerance = %+.2w
  FormatSpecUnderTolerance = %+.2w
  Inverted = false
  LineAngle = 0
  LockPosition = false
  MeasureType = 1
  OverTolerance = 0
  References2D = -> [ProjItem]
  Rotation = 0
  ScaleType = 0
  TheoreticalExact = false
  Type = 2
  UnderTolerance = 0
  X = 69.8038
  Y = 7.52223
FEATURE [TechDraw::DrawViewDimension] Dimension013
  AngleOverride = false
  Arbitrary = false
  ArbitraryTolerances = false
  EqualTolerance = true
  ExtensionAngle = 0
  FormatSpec = %.2w
  FormatSpecOverTolerance = %+.2w
  FormatSpecUnderTolerance = %+.2w
  Inverted = false
  LineAngle = 0
  LockPosition = false
  MeasureType = 1
  OverTolerance = 0
  References2D = -> [ProjItem]
  Rotation = 0
  ScaleType = 0
  TheoreticalExact = false
  Type = 1
  UnderTolerance = 0
  X = -0.579019
  Y = 34.1582
FEATURE [TechDraw::DrawViewDimension] Dimension014
  AngleOverride = false
  Arbitrary = false
  ArbitraryTolerances = false
  EqualTolerance = true
  ExtensionAngle = 0
  FormatSpec = %.2w
  FormatSpecOverTolerance = %+.2w
  FormatSpecUnderTolerance = %+.2w
  Inverted = false
  LineAngle = 0
  LockPosition = false
  MeasureType = 1
  OverTolerance = 0
  References2D = -> [ProjItem]
  Rotation = 0
  ScaleType = 0
  TheoreticalExact = false
  Type = 2
  UnderTolerance = 0
  X = -26.5869
  Y = -51.42
FEATURE [TechDraw::DrawViewDimension] Dimension015
  AngleOverride = false
  Arbitrary = false
  ArbitraryTolerances = false
  EqualTolerance = true
  ExtensionAngle = 0
  FormatSpec = %.2w
  FormatSpecOverTolerance = %+.2w
  FormatSpecUnderTolerance = %+.2w
  Inverted = false
  LineAngle = 0
  LockPosition = false
  MeasureType = 1
  OverTolerance = 0
  References2D = -> [ProjItem]
  Rotation = 0
  ScaleType = 0
  TheoreticalExact = false
  Type = 1
  UnderTolerance = 0
  X = -50.7857
  Y = -34.8412
FEATURE [TechDraw::DrawViewDimension] Dimension016
  AngleOverride = false
  Arbitrary = false
  ArbitraryTolerances = false
  EqualTolerance = true
  ExtensionAngle = 0
  FormatSpec = %.2w
  FormatSpecOverTolerance = %+.2w
  FormatSpecUnderTolerance = %+.2w
  Inverted = false
  LineAngle = 0
  LockPosition = false
  MeasureType = 1
  OverTolerance = 0
  References2D = -> [ProjItem]
  Rotation = 0
  ScaleType = 0
  TheoreticalExact = false
  Type = 2
  UnderTolerance = 0
  X = 37.8374
  Y = 30.1548
FEATURE [TechDraw::DrawViewDimension] Dimension017
  AngleOverride = false
  Arbitrary = false
  ArbitraryTolerances = false
  EqualTolerance = true
  ExtensionAngle = 0
  FormatSpec = %.2w
  FormatSpecOverTolerance = %+.2w
  FormatSpecUnderTolerance = %+.2w
  Inverted = false
  LineAngle = 0
  LockPosition = false
  MeasureType = 1
  OverTolerance = 0
  References2D = -> [ProjItem]
  Rotation = 0
  ScaleType = 0
  TheoreticalExact = false
  Type = 1
  UnderTolerance = 0
  X = 20.504
  Y = 38.2587
FEATURE [TechDraw::DrawViewDimension] Dimension018
  AngleOverride = false
  Arbitrary = false
  ArbitraryTolerances = false
  EqualTolerance = true
  ExtensionAngle = 0
  FormatSpec = %.2w
  FormatSpecOverTolerance = %+.2w
  FormatSpecUnderTolerance = %+.2w
  Inverted = false
  LineAngle = 0
  LockPosition = false
  MeasureType = 1
  OverTolerance = 0
  References2D = -> [ProjItem001]
  Rotation = 0
  ScaleType = 0
  TheoreticalExact = false
  Type = 1
  UnderTolerance = 0
  X = -12.5673
  Y = 35.3185
FEATURE [TechDraw::DrawViewDimension] Dimension019
  AngleOverride = false
  Arbitrary = false
  ArbitraryTolerances = false
  EqualTolerance = true
  ExtensionAngle = 0
  FormatSpec = %.2w
  FormatSpecOverTolerance = %+.2w
  FormatSpecUnderTolerance = %+.2w
  Inverted = false
  LineAngle = 0
  LockPosition = false
  MeasureType = 1
  OverTolerance = 0
  References2D = -> [ProjItem001]
  Rotation = 0
  ScaleType = 0
  TheoreticalExact = false
  Type = 1
  UnderTolerance = 0
  X = -0.664443
  Y = -30.733
FEATURE [TechDraw::DrawViewDimension] Dimension020
  AngleOverride = false
  Arbitrary = false
  ArbitraryTolerances = false
  EqualTolerance = true
  ExtensionAngle = 0
  FormatSpec = %.2w
  FormatSpecOverTolerance = %+.2w
  FormatSpecUnderTolerance = %+.2w
  Inverted = false
  LineAngle = 0
  LockPosition = false
  MeasureType = 1
  OverTolerance = 0
  References2D = -> [ProjItem002]
  Rotation = 0
  ScaleType = 0
  TheoreticalExact = false
  Type = 2
  UnderTolerance = 0
  X = -53.2297
  Y = 17.0274
FEATURE [TechDraw::DrawViewDimension] Dimension021
  AngleOverride = false
  Arbitrary = false
  ArbitraryTolerances = false
  EqualTolerance = true
  ExtensionAngle = 0
  FormatSpec = %.2w
  FormatSpecOverTolerance = %+.2w
  FormatSpecUnderTolerance = %+.2w
  Inverted = false
  LineAngle = 0
  LockPosition = false
  MeasureType = 1
  OverTolerance = 0
  References2D = -> [ProjItem002]
  Rotation = 0
  ScaleType = 0
  TheoreticalExact = false
  Type = 1
  UnderTolerance = 0
  X = -30.3235
  Y = -12.6197
FEATURE [TechDraw::DrawSVGTemplate] Template001
  EditableTexts = Designed_by_Name=Thomas Spielauer; FC-Date=2024-05-15; FC-SC=mm; FC-SH=1/1; FC-Title=Unshielded Kicker, 40mm; Subtitle=XL30 Column Mount, GNDPlane
  Height = 210
  Orientation = 1
  Template = <path>
  Width = 297
FEATURE [TechDraw::DrawProjGroupItem] ProjItem004  label="Front001"
  CoarseView = false
  Direction = (0,0,1)
  Focus = 100
  HardHidden = false
  IsoCount = 0
  IsoHidden = false
  IsoVisible = false
  LockPosition = true
  Perspective = false
  Rotation = 0
  RotationVector = (1,0,0)
  ScaleType = 2
  ScrubCount = 0
  SeamHidden = false
  SeamVisible = false
  SmoothHidden = false
  SmoothVisible = true
  Source = -> [Cut010]
  Type = 0
  X = 0
  XDirection = (1,0,0)
  Y = 0
FEATURE [TechDraw::DrawProjGroupItem] ProjItem005  label="Top001"
  CoarseView = false
  Direction = (0,1,0)
  Focus = 100
  HardHidden = false
  IsoCount = 0
  IsoHidden = false
  IsoVisible = false
  LockPosition = false
  Perspective = false
  Rotation = 0
  RotationVector = (1,0,0)
  ScaleType = 2
  ScrubCount = 0
  SeamHidden = false
  SeamVisible = false
  SmoothHidden = false
  SmoothVisible = true
  Source = -> [Cut010]
  Type = 4
  X = 0
  XDirection = (1,0,0)
  Y = -60.9623
FEATURE [TechDraw::DrawProjGroup] ProjGroup001
  Anchor = -> ProjItem004
  AutoDistribute = false
  LockPosition = false
  ProjectionType = 0
  Rotation = 0
  ScaleType = 0
  Source = -> [Cut010]
  Views = -> [ProjItem004,ProjItem005]
  X = 72.5036
  Y = 148.38
  spacingX = 15
  spacingY = 15
FEATURE [TechDraw::DrawViewDimension] Dimension022
  AngleOverride = false
  Arbitrary = false
  ArbitraryTolerances = false
  EqualTolerance = true
  ExtensionAngle = 0
  FormatSpec = %.2w
  FormatSpecOverTolerance = %+.2w
  FormatSpecUnderTolerance = %+.2w
  Inverted = false
  LineAngle = 0
  LockPosition = false
  MeasureType = 1
  OverTolerance = 0
  References2D = -> [ProjItem005]
  Rotation = 0
  ScaleType = 0
  TheoreticalExact = false
  Type = 2
  UnderTolerance = 0
  X = -32.2075
  Y = 10.4657
FEATURE [TechDraw::DrawViewDimension] Dimension023
  AngleOverride = false
  Arbitrary = false
  ArbitraryTolerances = false
  EqualTolerance = true
  ExtensionAngle = 0
  FormatSpec = %.2w
  FormatSpecOverTolerance = %+.2w
  FormatSpecUnderTolerance = %+.2w
  Inverted = false
  LineAngle = 0
  LockPosition = false
  MeasureType = 1
  OverTolerance = 0
  References2D = -> [ProjItem005]
  Rotation = 0
  ScaleType = 0
  TheoreticalExact = false
  Type = 1
  UnderTolerance = 0
  X = 29.1214
  Y = -0.481549
FEATURE [TechDraw::DrawViewDimension] Dimension024
  AngleOverride = false
  Arbitrary = false
  ArbitraryTolerances = false
  EqualTolerance = true
  ExtensionAngle = 0
  FormatSpec = %.2w
  FormatSpecOverTolerance = %+.2w
  FormatSpecUnderTolerance = %+.2w
  Inverted = false
  LineAngle = 0
  LockPosition = false
  MeasureType = 1
  OverTolerance = 0
  References2D = -> [ProjItem004]
  Rotation = 0
  ScaleType = 0
  TheoreticalExact = false
  Type = 1
  UnderTolerance = 0
  X = 0.591479
  Y = -25.7949
FEATURE [TechDraw::DrawViewDimension] Dimension025
  AngleOverride = false
  Arbitrary = false
  ArbitraryTolerances = false
  EqualTolerance = true
  ExtensionAngle = 0
  FormatSpec = %.2w
  FormatSpecOverTolerance = %+.2w
  FormatSpecUnderTolerance = %+.2w
  Inverted = false
  LineAngle = 0
  LockPosition = false
  MeasureType = 1
  OverTolerance = 0
  References2D = -> [ProjItem004]
  Rotation = 0
  ScaleType = 0
  TheoreticalExact = false
  Type = 2
  UnderTolerance = 0
  X = 27.9148
  Y = 2.30284
FEATURE [TechDraw::DrawViewDimension] Dimension026
  AngleOverride = false
  Arbitrary = false
  ArbitraryTolerances = false
  EqualTolerance = true
  ExtensionAngle = 0
  FormatSpec = ⌀%.2w (4x)
  FormatSpecOverTolerance = %+.2w
  FormatSpecUnderTolerance = %+.2w
  Inverted = false
  LineAngle = 0
  LockPosition = false
  MeasureType = 1
  OverTolerance = 0
  References2D = -> [ProjItem004]
  Rotation = 0
  ScaleType = 0
  TheoreticalExact = false
  Type = 5
  UnderTolerance = 0
  X = -47.7524
  Y = 11.7161
FEATURE [TechDraw::DrawViewDimension] Dimension027
  AngleOverride = false
  Arbitrary = false
  ArbitraryTolerances = false
  EqualTolerance = true
  ExtensionAngle = 0
  FormatSpec = ⌀%.2w (1x)
  FormatSpecOverTolerance = %+.2w
  FormatSpecUnderTolerance = %+.2w
  Inverted = false
  LineAngle = 0
  LockPosition = false
  MeasureType = 1
  OverTolerance = 0
  References2D = -> [ProjItem004]
  Rotation = 0
  ScaleType = 0
  TheoreticalExact = false
  Type = 5
  UnderTolerance = 0
  X = -47.2211
  Y = -4.60396
FEATURE [TechDraw::DrawViewDimension] Dimension028
  AngleOverride = false
  Arbitrary = false
  ArbitraryTolerances = false
  EqualTolerance = true
  ExtensionAngle = 0
  FormatSpec = %.2w
  FormatSpecOverTolerance = %+.2w
  FormatSpecUnderTolerance = %+.2w
  Inverted = false
  LineAngle = 0
  LockPosition = false
  MeasureType = 1
  OverTolerance = 0
  References2D = -> [ProjItem004]
  Rotation = 0
  ScaleType = 0
  TheoreticalExact = false
  Type = 2
  UnderTolerance = 0
  X = 37.2453
  Y = 31.5717
FEATURE [TechDraw::DrawViewDimension] Dimension029
  AngleOverride = false
  Arbitrary = false
  ArbitraryTolerances = false
  EqualTolerance = true
  ExtensionAngle = 0
  FormatSpec = %.2w
  FormatSpecOverTolerance = %+.2w
  FormatSpecUnderTolerance = %+.2w
  Inverted = false
  LineAngle = 0
  LockPosition = false
  MeasureType = 1
  OverTolerance = 0
  References2D = -> [ProjItem004]
  Rotation = 0
  ScaleType = 0
  TheoreticalExact = false
  Type = 1
  UnderTolerance = 0
  X = 10.0791
  Y = 41.6637
FEATURE [TechDraw::DrawViewDimension] Dimension030
  AngleOverride = false
  Arbitrary = false
  ArbitraryTolerances = false
  EqualTolerance = true
  ExtensionAngle = 0
  FormatSpec = %.2w
  FormatSpecOverTolerance = %+.2w
  FormatSpecUnderTolerance = %+.2w
  Inverted = false
  LineAngle = 0
  LockPosition = false
  MeasureType = 1
  OverTolerance = 0
  References2D = -> [ProjItem004]
  Rotation = 0
  ScaleType = 0
  TheoreticalExact = false
  Type = 1
  UnderTolerance = 0
  X = -5.59035
  Y = 37.971
FEATURE [TechDraw::DrawViewDimension] Dimension031
  AngleOverride = false
  Arbitrary = false
  ArbitraryTolerances = false
  EqualTolerance = true
  ExtensionAngle = 0
  FormatSpec = %.2w
  FormatSpecOverTolerance = %+.2w
  FormatSpecUnderTolerance = %+.2w
  Inverted = false
  LineAngle = 0
  LockPosition = false
  MeasureType = 1
  OverTolerance = 0
  References2D = -> [ProjItem004]
  Rotation = 0
  ScaleType = 0
  TheoreticalExact = false
  Type = 2
  UnderTolerance = 0
  X = -35.7836
  Y = 30.9806
FEATURE [TechDraw::DrawViewDimension] Dimension032
  AngleOverride = false
  Arbitrary = false
  ArbitraryTolerances = false
  EqualTolerance = true
  ExtensionAngle = 0
  FormatSpec = %.2w
  FormatSpecOverTolerance = %+.2w
  FormatSpecUnderTolerance = %+.2w
  Inverted = false
  LineAngle = 0
  LockPosition = false
  MeasureType = 1
  OverTolerance = 0
  References2D = -> [ProjItem004]
  Rotation = 0
  ScaleType = 0
  TheoreticalExact = false
  Type = 1
  UnderTolerance = 0
  X = -12.9287
  Y = -36.1563
FEATURE [TechDraw::DrawViewDimension] Dimension033
  AngleOverride = false
  Arbitrary = false
  ArbitraryTolerances = false
  EqualTolerance = true
  ExtensionAngle = 0
  FormatSpec = %.2w
  FormatSpecOverTolerance = %+.2w
  FormatSpecUnderTolerance = %+.2w
  Inverted = false
  LineAngle = 0
  LockPosition = false
  MeasureType = 1
  OverTolerance = 0
  References2D = -> [ProjItem004]
  Rotation = 0
  ScaleType = 0
  TheoreticalExact = false
  Type = 1
  UnderTolerance = 0
  X = 9.02528
  Y = -36.647
FEATURE [TechDraw::DrawViewDimension] Dimension034
  AngleOverride = false
  Arbitrary = false
  ArbitraryTolerances = false
  EqualTolerance = true
  ExtensionAngle = 0
  FormatSpec = %.2w
  FormatSpecOverTolerance = %+.2w
  FormatSpecUnderTolerance = %+.2w
  Inverted = false
  LineAngle = 0
  LockPosition = false
  MeasureType = 1
  OverTolerance = 0
  References2D = -> [ProjItem004]
  Rotation = 0
  ScaleType = 0
  TheoreticalExact = false
  Type = 2
  UnderTolerance = 0
  X = -31.2577
  Y = -26.0199
FEATURE [TechDraw::DrawViewDimension] Dimension035
  AngleOverride = false
  Arbitrary = false
  ArbitraryTolerances = false
  EqualTolerance = true
  ExtensionAngle = 0
  FormatSpec = %.2w
  FormatSpecOverTolerance = %+.2w
  FormatSpecUnderTolerance = %+.2w
  Inverted = false
  LineAngle = 0
  LockPosition = false
  MeasureType = 1
  OverTolerance = 0
  References2D = -> [ProjItem004]
  Rotation = 0
  ScaleType = 0
  TheoreticalExact = false
  Type = 2
  UnderTolerance = 0
  X = 34.6318
  Y = -25.2404
FEATURE [TechDraw::DrawViewDimension] Dimension036
  AngleOverride = false
  Arbitrary = false
  ArbitraryTolerances = false
  EqualTolerance = true
  ExtensionAngle = 0
  FormatSpec = %.2w
  FormatSpecOverTolerance = %+.2w
  FormatSpecUnderTolerance = %+.2w
  Inverted = false
  LineAngle = 0
  LockPosition = false
  MeasureType = 1
  OverTolerance = 0
  References2D = -> [ProjItem004]
  Rotation = 0
  ScaleType = 0
  TheoreticalExact = false
  Type = 1
  UnderTolerance = 0
  X = -3.30756
  Y = 50.3605
FEATURE [TechDraw::DrawViewDimension] Dimension037
  AngleOverride = false
  Arbitrary = false
  ArbitraryTolerances = false
  EqualTolerance = true
  ExtensionAngle = 0
  FormatSpec = %.2w
  FormatSpecOverTolerance = %+.2w
  FormatSpecUnderTolerance = %+.2w
  Inverted = false
  LineAngle = 0
  LockPosition = false
  MeasureType = 1
  OverTolerance = 0
  References2D = -> [ProjItem004]
  Rotation = 0
  ScaleType = 0
  TheoreticalExact = false
  Type = 2
  UnderTolerance = 0
  X = -1.64658
  Y = -7.64049
FEATURE [TechDraw::DrawViewAnnotation] Annotation
  Font = osifont
  LineSpace = 100
  LockPosition = false
  MaxWidth = -1
  Rotation = 0
  ScaleType = 0
  Text = Material: Copper | Thickness: not too critical
  TextSize = 5
  TextStyle = 0
  X = 240.881
  Y = 178.651
FEATURE [TechDraw::DrawPage] Page001  label="Page_GNDPlane"
  KeepUpdated = true
  NextBalloonIndex = 1
  ProjectionType = 0
  Template = -> Template001
  Views = -> [ProjGroup001,Dimension022,Dimension023,Dimension024,Dimension025,Dimension026,Dimension027,Dimension028,Dimension029,Dimension030,Dimension031,Dimension032,Dimension033,Dimension034,Dimension035,Dimension036,Dimension037,Annotation]
FEATURE [TechDraw::DrawViewAnnotation] Annotation001
  Font = osifont
  LineSpace = 100
  LockPosition = false
  MaxWidth = -1
  Rotation = 0
  ScaleType = 0
  Text = Material: Aluminium
  TextSize = 5
  TextStyle = 0
  X = 243.82
  Y = 82.2214
FEATURE [TechDraw::DrawPage] Page  label="Page_Holder"
  KeepUpdated = true
  NextBalloonIndex = 1
  ProjectionType = 0
  Template = -> Template
  Views = -> [ProjGroup,Dimension,Dimension001,Dimension002,Dimension003,Dimension004,Dimension005,Dimension006,Dimension007,Dimension008,Dimension009,Dimension010,Dimension011,Dimension012,Dimension013,Dimension014,Dimension015,Dimension016,Dimension017,Dimension018,Dimension019,Dimension020,Dimension021,Annotation001]
FEATURE [TechDraw::DrawSVGTemplate] Template002
  EditableTexts = Designed_by_Name=Thomas Spielauer; FC-Date=2024-05-15; FC-SC=mm; FC-SH=1/3; FC-Title=Unshielded kicker, 40mm; Subtitle=XL30 Column Mount, Part A
  Height = 210
  Orientation = 1
  Template = <path>
  Width = 297
FEATURE [TechDraw::DrawProjGroupItem] ProjItem006  label="Front002"
  CoarseView = false
  Direction = (1,0,0)
  Focus = 100
  HardHidden = false
  IsoCount = 0
  IsoHidden = false
  IsoVisible = false
  LockPosition = true
  Perspective = false
  Rotation = 0
  RotationVector = (0,0,-1)
  Scale = 3
  ScaleType = 2
  ScrubCount = 0
  SeamHidden = false
  SeamVisible = false
  SmoothHidden = false
  SmoothVisible = true
  Source = -> [Cut008]
  Type = 0
  X = 0
  XDirection = (0,0,-1)
  Y = 0
FEATURE [TechDraw::DrawProjGroupItem] ProjItem007  label="Left001"
  CoarseView = false
  Direction = (1e-16,0,1)
  Focus = 100
  HardHidden = false
  IsoCount = 0
  IsoHidden = false
  IsoVisible = false
  LockPosition = false
  Perspective = false
  Rotation = 0
  RotationVector = (1,0,0)
  Scale = 3
  ScaleType = 2
  ScrubCount = 0
  SeamHidden = false
  SeamVisible = false
  SmoothHidden = false
  SmoothVisible = true
  Source = -> [Cut008]
  Type = 1
  X = 130.101
  XDirection = (1,0,-1e-16)
  Y = 0
FEATURE [TechDraw::DrawProjGroupItem] ProjItem008  label="Bottom"
  CoarseView = false
  Direction = (0,-1,0)
  Focus = 100
  HardHidden = false
  IsoCount = 0
  IsoHidden = false
  IsoVisible = false
  LockPosition = false
  Perspective = false
  Rotation = 0
  RotationVector = (1,0,0)
  Scale = 3
  ScaleType = 2
  ScrubCount = 0
  SeamHidden = false
  SeamVisible = false
  SmoothHidden = false
  SmoothVisible = true
  Source = -> [Cut008]
  Type = 5
  X = 0
  XDirection = (0,0,-1)
  Y = 72.7718
FEATURE [TechDraw::DrawProjGroup] ProjGroup002
  Anchor = -> ProjItem006
  AutoDistribute = false
  LockPosition = false
  ProjectionType = 0
  Rotation = 0
  Scale = 3
  ScaleType = 2
  Source = -> [Cut008]
  Views = -> [ProjItem006,ProjItem007,ProjItem008]
  X = 110.07
  Y = 107.026
  spacingX = 15
  spacingY = 15
FEATURE [TechDraw::DrawViewDimension] Dimension038
  AngleOverride = false
  Arbitrary = false
  ArbitraryTolerances = false
  EqualTolerance = true
  ExtensionAngle = 0
  FormatSpec = %.2w
  FormatSpecOverTolerance = %+.2w
  FormatSpecUnderTolerance = %+.2w
  Inverted = false
  LineAngle = 0
  LockPosition = false
  MeasureType = 1
  OverTolerance = 0
  References2D = -> [ProjItem008]
  Rotation = 0
  ScaleType = 0
  TheoreticalExact = false
  Type = 1
  UnderTolerance = 0
  X = 88.7082
  Y = 18.7656
FEATURE [TechDraw::DrawViewDimension] Dimension039
  AngleOverride = false
  Arbitrary = false
  ArbitraryTolerances = false
  EqualTolerance = true
  ExtensionAngle = 0
  FormatSpec = %.2w
  FormatSpecOverTolerance = %+.2w
  FormatSpecUnderTolerance = %+.2w
  Inverted = false
  LineAngle = 0
  LockPosition = false
  MeasureType = 1
  OverTolerance = 0
  References2D = -> [ProjItem008]
  Rotation = 0
  ScaleType = 0
  TheoreticalExact = false
  Type = 2
  UnderTolerance = 0
  X = 82.001
  Y = -12.1674
FEATURE [TechDraw::DrawViewDimension] Dimension040
  AngleOverride = false
  Arbitrary = false
  ArbitraryTolerances = false
  EqualTolerance = true
  ExtensionAngle = 0
  FormatSpec = %.2w
  FormatSpecOverTolerance = %+.2w
  FormatSpecUnderTolerance = %+.2w
  Inverted = false
  LineAngle = 0
  LockPosition = false
  MeasureType = 1
  OverTolerance = 0
  References2D = -> [ProjItem007]
  Rotation = 0
  ScaleType = 0
  TheoreticalExact = false
  Type = 1
  UnderTolerance = 0
  X = 17.1769
  Y = 49.0017
FEATURE [TechDraw::DrawViewDimension] Dimension041
  AngleOverride = false
  Arbitrary = false
  ArbitraryTolerances = false
  EqualTolerance = true
  ExtensionAngle = 0
  FormatSpec = R%.2w
  FormatSpecOverTolerance = %+.2w
  FormatSpecUnderTolerance = %+.2w
  Inverted = false
  LineAngle = 0
  LockPosition = false
  MeasureType = 1
  OverTolerance = 0
  References2D = -> [ProjItem007]
  Rotation = 0
  ScaleType = 0
  TheoreticalExact = false
  Type = 4
  UnderTolerance = 0
  X = 19.4478
  Y = 17.4082
FEATURE [TechDraw::DrawViewDimension] Dimension042
  AngleOverride = false
  Arbitrary = false
  ArbitraryTolerances = false
  EqualTolerance = true
  ExtensionAngle = 0
  FormatSpec = %.2w
  FormatSpecOverTolerance = %+.2w
  FormatSpecUnderTolerance = %+.2w
  Inverted = false
  LineAngle = 0
  LockPosition = false
  MeasureType = 1
  OverTolerance = 0
  References2D = -> [ProjItem007]
  Rotation = 0
  ScaleType = 0
  TheoreticalExact = false
  Type = 1
  UnderTolerance = 0
  X = -1.84837
  Y = 57.8052
FEATURE [TechDraw::DrawViewDimension] Dimension043
  AngleOverride = false
  Arbitrary = false
  ArbitraryTolerances = false
  EqualTolerance = true
  ExtensionAngle = 0
  FormatSpec = %.2w
  FormatSpecOverTolerance = %+.2w
  FormatSpecUnderTolerance = %+.2w
  Inverted = false
  LineAngle = 0
  LockPosition = false
  MeasureType = 1
  OverTolerance = 0
  References2D = -> [ProjItem007]
  Rotation = 0
  ScaleType = 0
  TheoreticalExact = false
  Type = 2
  UnderTolerance = 0
  X = -13.2954
  Y = 2.5
FEATURE [TechDraw::DrawViewDimension] Dimension044
  AngleOverride = false
  Arbitrary = false
  ArbitraryTolerances = false
  EqualTolerance = true
  ExtensionAngle = 0
  FormatSpec = %.2w
  FormatSpecOverTolerance = %+.2w
  FormatSpecUnderTolerance = %+.2w
  Inverted = false
  LineAngle = 0
  LockPosition = false
  MeasureType = 1
  OverTolerance = 0
  References2D = -> [ProjItem006]
  Rotation = 0
  ScaleType = 0
  TheoreticalExact = false
  Type = 2
  UnderTolerance = 0
  X = 75.0421
  Y = 2.87141
FEATURE [TechDraw::DrawViewDimension] Dimension045
  AngleOverride = false
  Arbitrary = false
  ArbitraryTolerances = false
  EqualTolerance = true
  ExtensionAngle = 0
  FormatSpec = %.2w
  FormatSpecOverTolerance = %+.2w
  FormatSpecUnderTolerance = %+.2w
  Inverted = false
  LineAngle = 0
  LockPosition = false
  MeasureType = 1
  OverTolerance = 0
  References2D = -> [ProjItem007]
  Rotation = 0
  ScaleType = 0
  TheoreticalExact = false
  Type = 2
  UnderTolerance = 0
  X = 30.6805
  Y = 19.5715
FEATURE [TechDraw::DrawViewDimension] Dimension046
  AngleOverride = false
  Arbitrary = false
  ArbitraryTolerances = false
  EqualTolerance = true
  ExtensionAngle = 0
  FormatSpec = %.2w
  FormatSpecOverTolerance = %+.2w
  FormatSpecUnderTolerance = %+.2w
  Inverted = false
  LineAngle = 0
  LockPosition = false
  MeasureType = 1
  OverTolerance = 0
  References2D = -> [ProjItem006]
  Rotation = 0
  ScaleType = 0
  TheoreticalExact = false
  Type = 1
  UnderTolerance = 0
  X = 30.4505
  Y = 50.4642
FEATURE [TechDraw::DrawViewDimension] Dimension047
  AngleOverride = false
  Arbitrary = false
  ArbitraryTolerances = false
  EqualTolerance = true
  ExtensionAngle = 0
  FormatSpec = %.2w
  FormatSpecOverTolerance = %+.2w
  FormatSpecUnderTolerance = %+.2w
  Inverted = false
  LineAngle = 0
  LockPosition = false
  MeasureType = 1
  OverTolerance = 0
  References2D = -> [ProjItem006]
  Rotation = 0
  ScaleType = 0
  TheoreticalExact = false
  Type = 1
  UnderTolerance = 0
  X = -1.25939
  Y = 53.0599
FEATURE [TechDraw::DrawViewDimension] Dimension048
  AngleOverride = false
  Arbitrary = false
  ArbitraryTolerances = false
  EqualTolerance = true
  ExtensionAngle = 0
  FormatSpec = %.2w
  FormatSpecOverTolerance = %+.2w
  FormatSpecUnderTolerance = %+.2w
  Inverted = false
  LineAngle = 0
  LockPosition = false
  MeasureType = 1
  OverTolerance = 0
  References2D = -> [ProjItem006]
  Rotation = 0
  ScaleType = 0
  TheoreticalExact = false
  Type = 1
  UnderTolerance = 0
  X = -47.1559
  Y = -51.2102
FEATURE [TechDraw::DrawViewDimension] Dimension049
  AngleOverride = false
  Arbitrary = false
  ArbitraryTolerances = false
  EqualTolerance = true
  ExtensionAngle = 0
  FormatSpec = %.2w
  FormatSpecOverTolerance = %+.2w
  FormatSpecUnderTolerance = %+.2w
  Inverted = false
  LineAngle = 0
  LockPosition = false
  MeasureType = 1
  OverTolerance = 0
  References2D = -> [ProjItem006]
  Rotation = 0
  ScaleType = 0
  TheoreticalExact = false
  Type = 1
  UnderTolerance = 0
  X = -0.327967
  Y = -50.8822
FEATURE [TechDraw::DrawViewDimension] Dimension050
  AngleOverride = false
  Arbitrary = false
  ArbitraryTolerances = false
  EqualTolerance = true
  ExtensionAngle = 0
  FormatSpec = %.2w
  FormatSpecOverTolerance = %+.2w
  FormatSpecUnderTolerance = %+.2w
  Inverted = false
  LineAngle = 0
  LockPosition = false
  MeasureType = 1
  OverTolerance = 0
  References2D = -> [ProjItem006]
  Rotation = 0
  ScaleType = 0
  TheoreticalExact = false
  Type = 2
  UnderTolerance = 0
  X = -25.339
  Y = -18.7644
FEATURE [TechDraw::DrawViewDimension] Dimension051
  AngleOverride = false
  Arbitrary = false
  ArbitraryTolerances = false
  EqualTolerance = true
  ExtensionAngle = 0
  FormatSpec = ⌀%.2w
  FormatSpecOverTolerance = %+.2w
  FormatSpecUnderTolerance = %+.2w
  Inverted = false
  LineAngle = 0
  LockPosition = false
  MeasureType = 1
  OverTolerance = 0
  References2D = -> [ProjItem006]
  Rotation = 0
  ScaleType = 0
  TheoreticalExact = false
  Type = 5
  UnderTolerance = 0
  X = -52.9338
  Y = 62.6817
FEATURE [TechDraw::DrawViewDimension] Dimension052
  AngleOverride = false
  Arbitrary = false
  ArbitraryTolerances = false
  EqualTolerance = true
  ExtensionAngle = 0
  FormatSpec = ⌀%.2w
  FormatSpecOverTolerance = %+.2w
  FormatSpecUnderTolerance = %+.2w
  Inverted = false
  LineAngle = 0
  LockPosition = false
  MeasureType = 1
  OverTolerance = 0
  References2D = -> [ProjItem006]
  Rotation = 0
  ScaleType = 0
  TheoreticalExact = false
  Type = 5
  UnderTolerance = 0
  X = -65.9493
  Y = 61.1028
FEATURE [TechDraw::DrawViewDimension] Dimension053
  AngleOverride = false
  Arbitrary = false
  ArbitraryTolerances = false
  EqualTolerance = true
  ExtensionAngle = 0
  FormatSpec = %.2w
  FormatSpecOverTolerance = %+.2w
  FormatSpecUnderTolerance = %+.2w
  Inverted = false
  LineAngle = 0
  LockPosition = false
  MeasureType = 1
  OverTolerance = 0
  References2D = -> [ProjItem006]
  Rotation = 0
  ScaleType = 0
  TheoreticalExact = false
  Type = 1
  UnderTolerance = 0
  X = 40.5086
  Y = 58.4974
FEATURE [TechDraw::DrawViewDimension] Dimension054
  AngleOverride = false
  Arbitrary = false
  ArbitraryTolerances = false
  EqualTolerance = true
  ExtensionAngle = 0
  FormatSpec = %.2w
  FormatSpecOverTolerance = %+.2w
  FormatSpecUnderTolerance = %+.2w
  Inverted = false
  LineAngle = 0
  LockPosition = false
  MeasureType = 1
  OverTolerance = 0
  References2D = -> [ProjItem006]
  Rotation = 0
  ScaleType = 0
  TheoreticalExact = false
  Type = 1
  UnderTolerance = 0
  X = 69.22
  Y = 46.7974
FEATURE [TechDraw::DrawViewDimension] Dimension055
  AngleOverride = false
  Arbitrary = false
  ArbitraryTolerances = false
  EqualTolerance = true
  ExtensionAngle = 0
  FormatSpec = %.2w
  FormatSpecOverTolerance = %+.2w
  FormatSpecUnderTolerance = %+.2w
  Inverted = false
  LineAngle = 0
  LockPosition = false
  MeasureType = 1
  OverTolerance = 0
  References2D = -> [ProjItem006]
  Rotation = 0
  ScaleType = 0
  TheoreticalExact = false
  Type = 2
  UnderTolerance = 0
  X = 91.6481
  Y = 46.9183
FEATURE [TechDraw::DrawViewDimension] Dimension056
  AngleOverride = false
  Arbitrary = false
  ArbitraryTolerances = false
  EqualTolerance = true
  ExtensionAngle = 0
  FormatSpec = %.2w
  FormatSpecOverTolerance = %+.2w
  FormatSpecUnderTolerance = %+.2w
  Inverted = false
  LineAngle = 0
  LockPosition = false
  MeasureType = 1
  OverTolerance = 0
  References2D = -> [ProjItem006]
  Rotation = 0
  ScaleType = 0
  TheoreticalExact = false
  Type = 2
  UnderTolerance = 0
  X = 102.211
  Y = 46.8249
FEATURE [TechDraw::DrawViewDimension] Dimension057
  AngleOverride = false
  Arbitrary = false
  ArbitraryTolerances = false
  EqualTolerance = true
  ExtensionAngle = 0
  FormatSpec = %.2w
  FormatSpecOverTolerance = %+.2w
  FormatSpecUnderTolerance = %+.2w
  Inverted = false
  LineAngle = 0
  LockPosition = false
  MeasureType = 1
  OverTolerance = 0
  References2D = -> [ProjItem006]
  Rotation = 0
  ScaleType = 0
  TheoreticalExact = false
  Type = 1
  UnderTolerance = 0
  X = -81.1028
  Y = 47.1887
FEATURE [TechDraw::DrawViewDimension] Dimension058
  AngleOverride = false
  Arbitrary = false
  ArbitraryTolerances = false
  EqualTolerance = true
  ExtensionAngle = 0
  FormatSpec = %.2w
  FormatSpecOverTolerance = %+.2w
  FormatSpecUnderTolerance = %+.2w
  Inverted = false
  LineAngle = 0
  LockPosition = false
  MeasureType = 1
  OverTolerance = 0
  References2D = -> [ProjItem006]
  Rotation = 0
  ScaleType = 0
  TheoreticalExact = false
  Type = 1
  UnderTolerance = 0
  X = -80.8937
  Y = 56.3144
FEATURE [TechDraw::DrawViewDimension] Dimension059
  AngleOverride = false
  Arbitrary = false
  ArbitraryTolerances = false
  EqualTolerance = true
  ExtensionAngle = 0
  FormatSpec = %.2w
  FormatSpecOverTolerance = %+.2w
  FormatSpecUnderTolerance = %+.2w
  Inverted = false
  LineAngle = 0
  LockPosition = false
  MeasureType = 1
  OverTolerance = 0
  References2D = -> [ProjItem006]
  Rotation = 0
  ScaleType = 0
  TheoreticalExact = false
  Type = 2
  UnderTolerance = 0
  X = -86.34
  Y = 29.3681
FEATURE [TechDraw::DrawViewDimension] Dimension060
  AngleOverride = false
  Arbitrary = false
  ArbitraryTolerances = false
  EqualTolerance = true
  ExtensionAngle = 0
  FormatSpec = %.2w
  FormatSpecOverTolerance = %+.2w
  FormatSpecUnderTolerance = %+.2w
  Inverted = false
  LineAngle = 0
  LockPosition = false
  MeasureType = 1
  OverTolerance = 0
  References2D = -> [ProjItem006]
  Rotation = 0
  ScaleType = 0
  TheoreticalExact = false
  Type = 2
  UnderTolerance = 0
  X = -74.8925
  Y = 30.9455
FEATURE [TechDraw::DrawViewDimension] Dimension061
  AngleOverride = false
  Arbitrary = false
  ArbitraryTolerances = false
  EqualTolerance = true
  ExtensionAngle = 0
  FormatSpec = %.2w
  FormatSpecOverTolerance = %+.2w
  FormatSpecUnderTolerance = %+.2w
  Inverted = false
  LineAngle = 0
  LockPosition = false
  MeasureType = 1
  OverTolerance = 0
  References2D = -> [ProjItem006]
  Rotation = 0
  ScaleType = 0
  TheoreticalExact = false
  Type = 1
  UnderTolerance = 0
  X = -67.2759
  Y = -40.6709
FEATURE [TechDraw::DrawViewDimension] Dimension062
  AngleOverride = false
  Arbitrary = false
  ArbitraryTolerances = false
  EqualTolerance = true
  ExtensionAngle = 0
  FormatSpec = %.2w
  FormatSpecOverTolerance = %+.2w
  FormatSpecUnderTolerance = %+.2w
  Inverted = false
  LineAngle = 0
  LockPosition = false
  MeasureType = 1
  OverTolerance = 0
  References2D = -> [ProjItem006]
  Rotation = 0
  ScaleType = 0
  TheoreticalExact = false
  Type = 2
  UnderTolerance = 0
  X = -75.2153
  Y = -22.0202
FEATURE [TechDraw::DrawViewDimension] Dimension063
  AngleOverride = false
  Arbitrary = false
  ArbitraryTolerances = false
  EqualTolerance = true
  ExtensionAngle = 0
  FormatSpec = %.2w
  FormatSpecOverTolerance = %+.2w
  FormatSpecUnderTolerance = %+.2w
  Inverted = false
  LineAngle = 0
  LockPosition = false
  MeasureType = 1
  OverTolerance = 0
  References2D = -> [ProjItem006]
  Rotation = 0
  ScaleType = 0
  TheoreticalExact = false
  Type = 2
  UnderTolerance = 0
  X = -96.8517
  Y = 18.4352
FEATURE [TechDraw::DrawSVGTemplate] Template003
  EditableTexts = Designed_by_Name=Thomas Spielauer; FC-Date=2024-05-15; FC-SC=mm; FC-SH=2/3; FC-Title=Unshielded kicker, 40mm; Subtitle=XL30 Column Mount, Part A
  Height = 210
  Orientation = 1
  Template = <path>
  Width = 297
FEATURE [TechDraw::DrawViewPart] View
  CoarseView = false
  Direction = (1,0,0)
  Focus = 100
  HardHidden = false
  IsoCount = 0
  IsoHidden = false
  IsoVisible = false
  LockPosition = false
  Perspective = false
  Rotation = 0
  Scale = 2
  ScaleType = 2
  ScrubCount = 0
  SeamHidden = false
  SeamVisible = false
  SmoothHidden = false
  SmoothVisible = true
  Source = -> [Cut008]
  X = 81.5636
  XDirection = (0,0,-1)
  Y = 151.63
FEATURE [TechDraw::DrawViewSection] SectionView  label="Section  - "
  BaseView = -> View
  CoarseView = false
  CutSurfaceDisplay = 2
  Direction = (0,-1e-16,1)
  FileGeomPattern = <path>
  FileHatchPattern = <path>
  Focus = 100
  FuseBeforeCut = false
  HardHidden = false
  HatchOffset = (0,0,0)
  HatchRotation = 0
  HatchScale = 1
  IsoCount = 0
  IsoHidden = false
  IsoVisible = false
  LockPosition = false
  NameGeomPattern = Diamond
  Perspective = false
  Rotation = -90
  Scale = 4
  ScaleType = 2
  ScrubCount = 0
  SeamHidden = false
  SeamVisible = false
  SectionDirection = 4
  SectionLineStretch = 1
  SectionNormal = (0,-1e-16,1)
  SectionOrigin = (-1.87,0,45.25)
  SmoothHidden = false
  SmoothVisible = true
  Source = -> [Cut008]
  TrimAfterCut = false
  UsePreviousCut = false
  X = 182.892
  XDirection = (0,-1,-1e-16)
  Y = 120.425
FEATURE [TechDraw::DrawViewDimension] Dimension064
  AngleOverride = false
  Arbitrary = false
  ArbitraryTolerances = false
  EqualTolerance = true
  ExtensionAngle = 0
  FormatSpec = %.2w
  FormatSpecOverTolerance = %+.2w
  FormatSpecUnderTolerance = %+.2w
  Inverted = false
  LineAngle = 0
  LockPosition = false
  MeasureType = 1
  OverTolerance = 0
  References2D = -> [SectionView]
  Rotation = 0
  ScaleType = 0
  TheoreticalExact = false
  Type = 2
  UnderTolerance = 0
  X = 21.7177
  Y = 25.2376
FEATURE [TechDraw::DrawViewDimension] Dimension065
  AngleOverride = false
  Arbitrary = false
  ArbitraryTolerances = false
  EqualTolerance = true
  ExtensionAngle = 0
  FormatSpec = %.2w
  FormatSpecOverTolerance = %+.2w
  FormatSpecUnderTolerance = %+.2w
  Inverted = false
  LineAngle = 0
  LockPosition = false
  MeasureType = 1
  OverTolerance = 0
  References2D = -> [SectionView]
  Rotation = 0
  ScaleType = 0
  TheoreticalExact = false
  Type = 2
  UnderTolerance = 0
  X = -22.6394
  Y = 25.9218
FEATURE [TechDraw::DrawViewDimension] Dimension066
  AngleOverride = false
  Arbitrary = false
  ArbitraryTolerances = false
  EqualTolerance = true
  ExtensionAngle = 0
  FormatSpec = %.2w
  FormatSpecOverTolerance = %+.2w
  FormatSpecUnderTolerance = %+.2w
  Inverted = false
  LineAngle = 0
  LockPosition = false
  MeasureType = 1
  OverTolerance = 0
  References2D = -> [SectionView]
  Rotation = 0
  ScaleType = 0
  TheoreticalExact = false
  Type = 1
  UnderTolerance = 0
  X = 15.5868
  Y = 60.8436
FEATURE [TechDraw::DrawViewDimension] Dimension067
  AngleOverride = false
  Arbitrary = false
  ArbitraryTolerances = false
  EqualTolerance = true
  ExtensionAngle = 0
  FormatSpec = %.2w
  FormatSpecOverTolerance = %+.2w
  FormatSpecUnderTolerance = %+.2w
  Inverted = false
  LineAngle = 0
  LockPosition = false
  MeasureType = 1
  OverTolerance = 0
  References2D = -> [SectionView]
  Rotation = 0
  ScaleType = 0
  TheoreticalExact = false
  Type = 1
  UnderTolerance = 0
  X = 15.8915
  Y = 70.1587
FEATURE [TechDraw::DrawViewDimension] Dimension068
  AngleOverride = false
  Arbitrary = false
  ArbitraryTolerances = false
  EqualTolerance = true
  ExtensionAngle = 0
  FormatSpec = %.2w
  FormatSpecOverTolerance = %+.2w
  FormatSpecUnderTolerance = %+.2w
  Inverted = false
  LineAngle = 0
  LockPosition = false
  MeasureType = 1
  OverTolerance = 0
  References2D = -> [SectionView]
  Rotation = 0
  ScaleType = 0
  TheoreticalExact = false
  Type = 1
  UnderTolerance = 0
  X = 11.0753
  Y = 78.4502
FEATURE [TechDraw::DrawPage] Page003  label="Page_CopperA_2"
  KeepUpdated = true
  NextBalloonIndex = 1
  ProjectionType = 0
  Template = -> Template003
  Views = -> [View,SectionView,Dimension064,Dimension065,Dimension066,Dimension067,Dimension068]
FEATURE [TechDraw::DrawSVGTemplate] Template004
  EditableTexts = Designed_by_Name=Thomas Spielauer; FC-Date=2024-05-15; FC-SC=mm; FC-SH=3/3; FC-Title=Unshielded kicker, 40mm; Subtitle=XL30 Column Mount, Part A
  Height = 210
  Orientation = 1
  Template = <path>
  Width = 297
FEATURE [TechDraw::DrawViewPart] View001
  CoarseView = false
  Direction = (1,0,0)
  Focus = 100
  HardHidden = false
  IsoCount = 0
  IsoHidden = false
  IsoVisible = false
  LockPosition = false
  Perspective = false
  Rotation = 0
  Scale = 3
  ScaleType = 2
  ScrubCount = 0
  SeamHidden = false
  SeamVisible = false
  SmoothHidden = false
  SmoothVisible = true
  Source = -> [Cut008]
  X = 142.087
  XDirection = (0,0,-1)
  Y = 148.184
FEATURE [TechDraw::DrawViewSection] SectionView001  label="Section001  - "
  BaseView = -> View001
  CoarseView = false
  CutSurfaceDisplay = 2
  Direction = (0,1,-1e-16)
  FileGeomPattern = <path>
  FileHatchPattern = <path>
  Focus = 100
  FuseBeforeCut = false
  HardHidden = false
  HatchOffset = (0,0,0)
  HatchRotation = 0
  HatchScale = 1
  IsoCount = 0
  IsoHidden = false
  IsoVisible = false
  LockPosition = false
  NameGeomPattern = Diamond
  Perspective = false
  Rotation = 0
  Scale = 4
  ScaleType = 2
  ScrubCount = 0
  SeamHidden = false
  SeamVisible = false
  SectionDirection = 4
  SectionLineStretch = 1
  SectionNormal = (0,1,-1e-16)
  SectionOrigin = (-1.87,7.5,28)
  SmoothHidden = false
  SmoothVisible = true
  Source = -> [Cut008]
  TrimAfterCut = false
  UsePreviousCut = false
  X = 145.485
  XDirection = (0,-1e-16,-1)
  Y = 86.4085
FEATURE [TechDraw::DrawViewDimension] Dimension069
  AngleOverride = false
  Arbitrary = false
  ArbitraryTolerances = false
  EqualTolerance = true
  ExtensionAngle = 0
  FormatSpec = %.2w
  FormatSpecOverTolerance = %+.2w
  FormatSpecUnderTolerance = %+.2w
  Inverted = false
  LineAngle = 0
  LockPosition = false
  MeasureType = 1
  OverTolerance = 0
  References2D = -> [SectionView001]
  Rotation = 0
  ScaleType = 0
  TheoreticalExact = false
  Type = 1
  UnderTolerance = 0
  X = -28.6727
  Y = -29.1711
FEATURE [TechDraw::DrawViewDimension] Dimension070
  AngleOverride = false
  Arbitrary = false
  ArbitraryTolerances = false
  EqualTolerance = true
  ExtensionAngle = 0
  FormatSpec = %.2w
  FormatSpecOverTolerance = %+.2w
  FormatSpecUnderTolerance = %+.2w
  Inverted = false
  LineAngle = 0
  LockPosition = false
  MeasureType = 1
  OverTolerance = 0
  References2D = -> [SectionView001]
  Rotation = 0
  ScaleType = 0
  TheoreticalExact = false
  Type = 1
  UnderTolerance = 0
  X = -30.2915
  Y = -18.1153
FEATURE [TechDraw::DrawViewDimension] Dimension071
  AngleOverride = false
  Arbitrary = false
  ArbitraryTolerances = false
  EqualTolerance = true
  ExtensionAngle = 0
  FormatSpec = %.2w
  FormatSpecOverTolerance = %+.2w
  FormatSpecUnderTolerance = %+.2w
  Inverted = false
  LineAngle = 0
  LockPosition = false
  MeasureType = 1
  OverTolerance = 0
  References2D = -> [SectionView001]
  Rotation = 0
  ScaleType = 0
  TheoreticalExact = false
  Type = 2
  UnderTolerance = 0
  X = -101.719
  Y = -12.5459
FEATURE [TechDraw::DrawViewDimension] Dimension072
  AngleOverride = false
  Arbitrary = false
  ArbitraryTolerances = false
  EqualTolerance = true
  ExtensionAngle = 0
  FormatSpec = %.2w
  FormatSpecOverTolerance = %+.2w
  FormatSpecUnderTolerance = %+.2w
  Inverted = false
  LineAngle = 0
  LockPosition = false
  MeasureType = 1
  OverTolerance = 0
  References2D = -> [SectionView001]
  Rotation = 0
  ScaleType = 0
  TheoreticalExact = false
  Type = 2
  UnderTolerance = 0
  X = -91.8723
  Y = 16.7296
FEATURE [TechDraw::DrawPage] Page004  label="Page_CopperA_3"
  KeepUpdated = true
  NextBalloonIndex = 1
  ProjectionType = 0
  Template = -> Template004
  Views = -> [View001,SectionView001,Dimension069,Dimension070,Dimension071,Dimension072]
FEATURE [TechDraw::DrawSVGTemplate] Template005
  EditableTexts = Designed_by_Name=Thomas Spielauer; FC-Date=2024-05-15; FC-SC=mm; FC-SH=1/3; FC-Title=Unshielded kicker, 40mm; Subtitle=XL30 Column Mount, Part B
  Height = 210
  Orientation = 1
  Template = <path>
  Width = 297
FEATURE [TechDraw::DrawProjGroupItem] ProjItem009  label="Front003"
  CoarseView = false
  Direction = (-1,0,0)
  Focus = 100
  HardHidden = false
  IsoCount = 0
  IsoHidden = false
  IsoVisible = false
  LockPosition = true
  Perspective = false
  Rotation = 0
  RotationVector = (0,0,1)
  Scale = 2
  ScaleType = 2
  ScrubCount = 0
  SeamHidden = false
  SeamVisible = false
  SmoothHidden = false
  SmoothVisible = true
  Source = -> [Cut006]
  Type = 0
  X = 0
  XDirection = (0,0,1)
  Y = 0
FEATURE [TechDraw::DrawProjGroupItem] ProjItem010  label="Bottom001"
  CoarseView = false
  Direction = (0,-1,0)
  Focus = 100
  HardHidden = false
  IsoCount = 0
  IsoHidden = false
  IsoVisible = false
  LockPosition = false
  Perspective = false
  Rotation = 0
  RotationVector = (1,0,0)
  Scale = 2
  ScaleType = 2
  ScrubCount = 0
  SeamHidden = false
  SeamVisible = false
  SmoothHidden = false
  SmoothVisible = true
  Source = -> [Cut006]
  Type = 5
  X = 0
  XDirection = (0,0,1)
  Y = 71.4762
FEATURE [TechDraw::DrawProjGroupItem] ProjItem011  label="Left002"
  CoarseView = false
  Direction = (-1e-16,0,-1)
  Focus = 100
  HardHidden = false
  IsoCount = 0
  IsoHidden = false
  IsoVisible = false
  LockPosition = false
  Perspective = false
  Rotation = 0
  RotationVector = (1,0,0)
  Scale = 2
  ScaleType = 2
  ScrubCount = 0
  SeamHidden = false
  SeamVisible = false
  SmoothHidden = false
  SmoothVisible = true
  Source = -> [Cut006]
  Type = 1
  X = 100.39
  XDirection = (-1,0,1e-16)
  Y = 0
FEATURE [TechDraw::DrawProjGroup] ProjGroup003
  Anchor = -> ProjItem009
  AutoDistribute = false
  LockPosition = false
  ProjectionType = 0
  Rotation = 0
  Scale = 2
  ScaleType = 2
  Source = -> [Cut006]
  Views = -> [ProjItem009,ProjItem010,ProjItem011]
  X = 88.6924
  Y = 100.8
  spacingX = 15
  spacingY = 15
FEATURE [TechDraw::DrawViewDimension] Dimension073
  AngleOverride = false
  Arbitrary = false
  ArbitraryTolerances = false
  EqualTolerance = true
  ExtensionAngle = 0
  FormatSpec = %.2w
  FormatSpecOverTolerance = %+.2w
  FormatSpecUnderTolerance = %+.2w
  Inverted = false
  LineAngle = 0
  LockPosition = false
  MeasureType = 1
  OverTolerance = 0
  References2D = -> [ProjItem010]
  Rotation = 0
  ScaleType = 0
  TheoreticalExact = false
  Type = 1
  UnderTolerance = 0
  X = 55.5034
  Y = 18.5021
FEATURE [TechDraw::DrawViewDimension] Dimension074
  AngleOverride = false
  Arbitrary = false
  ArbitraryTolerances = false
  EqualTolerance = true
  ExtensionAngle = 0
  FormatSpec = %.2w
  FormatSpecOverTolerance = %+.2w
  FormatSpecUnderTolerance = %+.2w
  Inverted = false
  LineAngle = 0
  LockPosition = false
  MeasureType = 1
  OverTolerance = 0
  References2D = -> [ProjItem010]
  Rotation = 0
  ScaleType = 0
  TheoreticalExact = false
  Type = 2
  UnderTolerance = 0
  X = 71.5407
  Y = 14.5838
FEATURE [TechDraw::DrawViewDimension] Dimension075
  AngleOverride = false
  Arbitrary = false
  ArbitraryTolerances = false
  EqualTolerance = true
  ExtensionAngle = 0
  FormatSpec = %.2w
  FormatSpecOverTolerance = %+.2w
  FormatSpecUnderTolerance = %+.2w
  Inverted = false
  LineAngle = 0
  LockPosition = false
  MeasureType = 1
  OverTolerance = 0
  References2D = -> [ProjItem009]
  Rotation = 0
  ScaleType = 0
  TheoreticalExact = false
  Type = 1
  UnderTolerance = 0
  X = -28.7565
  Y = 51.1672
FEATURE [TechDraw::DrawViewDimension] Dimension076
  AngleOverride = false
  Arbitrary = false
  ArbitraryTolerances = false
  EqualTolerance = true
  ExtensionAngle = 0
  FormatSpec = %.2w
  FormatSpecOverTolerance = %+.2w
  FormatSpecUnderTolerance = %+.2w
  Inverted = false
  LineAngle = 0
  LockPosition = false
  MeasureType = 1
  OverTolerance = 0
  References2D = -> [ProjItem009]
  Rotation = 0
  ScaleType = 0
  TheoreticalExact = false
  Type = 1
  UnderTolerance = 0
  X = 22.7454
  Y = 51.3275
FEATURE [TechDraw::DrawViewDimension] Dimension077
  AngleOverride = false
  Arbitrary = false
  ArbitraryTolerances = false
  EqualTolerance = true
  ExtensionAngle = 0
  FormatSpec = %.2w
  FormatSpecOverTolerance = %+.2w
  FormatSpecUnderTolerance = %+.2w
  Inverted = false
  LineAngle = 0
  LockPosition = false
  MeasureType = 1
  OverTolerance = 0
  References2D = -> [ProjItem009]
  Rotation = 0
  ScaleType = 0
  TheoreticalExact = false
  Type = 2
  UnderTolerance = 0
  X = 56.9045
  Y = 1.04348
FEATURE [TechDraw::DrawViewDimension] Dimension078
  AngleOverride = false
  Arbitrary = false
  ArbitraryTolerances = false
  EqualTolerance = true
  ExtensionAngle = 0
  FormatSpec = %.2w
  FormatSpecOverTolerance = %+.2w
  FormatSpecUnderTolerance = %+.2w
  Inverted = false
  LineAngle = 0
  LockPosition = false
  MeasureType = 1
  OverTolerance = 0
  References2D = -> [ProjItem009]
  Rotation = 0
  ScaleType = 0
  TheoreticalExact = false
  Type = 2
  UnderTolerance = 0
  X = 53.4533
  Y = 17.2114
FEATURE [TechDraw::DrawViewDimension] Dimension079
  AngleOverride = false
  Arbitrary = false
  ArbitraryTolerances = false
  EqualTolerance = true
  ExtensionAngle = 0
  FormatSpec = %.2w
  FormatSpecOverTolerance = %+.2w
  FormatSpecUnderTolerance = %+.2w
  Inverted = false
  LineAngle = 0
  LockPosition = false
  MeasureType = 1
  OverTolerance = 0
  References2D = -> [ProjItem009]
  Rotation = 0
  ScaleType = 0
  TheoreticalExact = false
  Type = 2
  UnderTolerance = 0
  X = 45.9559
  Y = -11.0736
FEATURE [TechDraw::DrawViewDimension] Dimension080
  AngleOverride = false
  Arbitrary = false
  ArbitraryTolerances = false
  EqualTolerance = true
  ExtensionAngle = 0
  FormatSpec = %.2w
  FormatSpecOverTolerance = %+.2w
  FormatSpecUnderTolerance = %+.2w
  Inverted = false
  LineAngle = 0
  LockPosition = false
  MeasureType = 1
  OverTolerance = 0
  References2D = -> [ProjItem009]
  Rotation = 0
  ScaleType = 0
  TheoreticalExact = false
  Type = 2
  UnderTolerance = 0
  X = -17.2935
  Y = -12.9279
FEATURE [TechDraw::DrawViewDimension] Dimension081
  AngleOverride = false
  Arbitrary = false
  ArbitraryTolerances = false
  EqualTolerance = true
  ExtensionAngle = 0
  FormatSpec = %.2w
  FormatSpecOverTolerance = %+.2w
  FormatSpecUnderTolerance = %+.2w
  Inverted = false
  LineAngle = 0
  LockPosition = false
  MeasureType = 1
  OverTolerance = 0
  References2D = -> [ProjItem009]
  Rotation = 0
  ScaleType = 0
  TheoreticalExact = false
  Type = 1
  UnderTolerance = 0
  X = -31
  Y = -29.9681
FEATURE [TechDraw::DrawViewDimension] Dimension082
  AngleOverride = false
  Arbitrary = false
  ArbitraryTolerances = false
  EqualTolerance = true
  ExtensionAngle = 0
  FormatSpec = %.2w
  FormatSpecOverTolerance = %+.2w
  FormatSpecUnderTolerance = %+.2w
  Inverted = false
  LineAngle = 0
  LockPosition = false
  MeasureType = 1
  OverTolerance = 0
  References2D = -> [ProjItem009]
  Rotation = 0
  ScaleType = 0
  TheoreticalExact = false
  Type = 1
  UnderTolerance = 0
  X = 30.5543
  Y = -31.3052
FEATURE [TechDraw::DrawViewDimension] Dimension083
  AngleOverride = false
  Arbitrary = false
  ArbitraryTolerances = false
  EqualTolerance = true
  ExtensionAngle = 0
  FormatSpec = %.2w
  FormatSpecOverTolerance = %+.2w
  FormatSpecUnderTolerance = %+.2w
  Inverted = false
  LineAngle = 0
  LockPosition = false
  MeasureType = 1
  OverTolerance = 0
  References2D = -> [ProjItem009]
  Rotation = 0
  ScaleType = 0
  TheoreticalExact = false
  Type = 2
  UnderTolerance = 0
  X = 44.1979
  Y = 16.1398
FEATURE [TechDraw::DrawViewDimension] Dimension084
  AngleOverride = false
  Arbitrary = false
  ArbitraryTolerances = false
  EqualTolerance = true
  ExtensionAngle = 0
  FormatSpec = ⌀%.2w (2x)
  FormatSpecOverTolerance = %+.2w
  FormatSpecUnderTolerance = %+.2w
  Inverted = false
  LineAngle = 0
  LockPosition = false
  MeasureType = 1
  OverTolerance = 0
  References2D = -> [ProjItem009]
  Rotation = 0
  ScaleType = 0
  TheoreticalExact = false
  Type = 5
  UnderTolerance = 0
  X = -55.1948
  Y = 43.5748
FEATURE [TechDraw::DrawViewDimension] Dimension085
  AngleOverride = false
  Arbitrary = false
  ArbitraryTolerances = false
  EqualTolerance = true
  ExtensionAngle = 0
  FormatSpec = %.2w
  FormatSpecOverTolerance = %+.2w
  FormatSpecUnderTolerance = %+.2w
  Inverted = false
  LineAngle = 0
  LockPosition = false
  MeasureType = 1
  OverTolerance = 0
  References2D = -> [ProjItem011]
  Rotation = 0
  ScaleType = 0
  TheoreticalExact = false
  Type = 1
  UnderTolerance = 0
  X = 9.95465
  Y = 36.9177
FEATURE [TechDraw::DrawViewDimension] Dimension086
  AngleOverride = false
  Arbitrary = false
  ArbitraryTolerances = false
  EqualTolerance = true
  ExtensionAngle = 0
  FormatSpec = R%.2w
  FormatSpecOverTolerance = %+.2w
  FormatSpecUnderTolerance = %+.2w
  Inverted = false
  LineAngle = 0
  LockPosition = false
  MeasureType = 1
  OverTolerance = 0
  References2D = -> [ProjItem011]
  Rotation = 0
  ScaleType = 0
  TheoreticalExact = false
  Type = 4
  UnderTolerance = 0
  X = 22.03
  Y = 14.5931
FEATURE [TechDraw::DrawViewDimension] Dimension087
  AngleOverride = false
  Arbitrary = false
  ArbitraryTolerances = false
  EqualTolerance = true
  ExtensionAngle = 0
  FormatSpec = %.2w
  FormatSpecOverTolerance = %+.2w
  FormatSpecUnderTolerance = %+.2w
  Inverted = false
  LineAngle = 0
  LockPosition = false
  MeasureType = 1
  OverTolerance = 0
  References2D = -> [ProjItem011]
  Rotation = 0
  ScaleType = 0
  TheoreticalExact = false
  Type = 1
  UnderTolerance = 0
  X = 16.8382
  Y = -24.3064
FEATURE [TechDraw::DrawViewDimension] Dimension088
  AngleOverride = false
  Arbitrary = false
  ArbitraryTolerances = false
  EqualTolerance = true
  ExtensionAngle = 0
  FormatSpec = %.2w
  FormatSpecOverTolerance = %+.2w
  FormatSpecUnderTolerance = %+.2w
  Inverted = false
  LineAngle = 0
  LockPosition = false
  MeasureType = 1
  OverTolerance = 0
  References2D = -> [ProjItem011]
  Rotation = 0
  ScaleType = 0
  TheoreticalExact = false
  Type = 2
  UnderTolerance = 0
  X = -14.4755
  Y = 4.32414
FEATURE [TechDraw::DrawViewDimension] Dimension089
  AngleOverride = false
  Arbitrary = false
  ArbitraryTolerances = false
  EqualTolerance = true
  ExtensionAngle = 0
  FormatSpec = %.2w
  FormatSpecOverTolerance = %+.2w
  FormatSpecUnderTolerance = %+.2w
  Inverted = false
  LineAngle = 0
  LockPosition = false
  MeasureType = 1
  OverTolerance = 0
  References2D = -> [ProjItem009]
  Rotation = 0
  ScaleType = 0
  TheoreticalExact = false
  Type = 1
  UnderTolerance = 0
  X = -26.6929
  Y = 42.1989
FEATURE [TechDraw::DrawViewDimension] Dimension090
  AngleOverride = false
  Arbitrary = false
  ArbitraryTolerances = false
  EqualTolerance = true
  ExtensionAngle = 0
  FormatSpec = %.2w
  FormatSpecOverTolerance = %+.2w
  FormatSpecUnderTolerance = %+.2w
  Inverted = false
  LineAngle = 0
  LockPosition = false
  MeasureType = 1
  OverTolerance = 0
  References2D = -> [ProjItem009]
  Rotation = 0
  ScaleType = 0
  TheoreticalExact = false
  Type = 1
  UnderTolerance = 0
  X = -26.2574
  Y = 34.2309
FEATURE [TechDraw::DrawViewDimension] Dimension091
  AngleOverride = false
  Arbitrary = false
  ArbitraryTolerances = false
  EqualTolerance = true
  ExtensionAngle = 0
  FormatSpec = %.2w
  FormatSpecOverTolerance = %+.2w
  FormatSpecUnderTolerance = %+.2w
  Inverted = false
  LineAngle = 0
  LockPosition = false
  MeasureType = 1
  OverTolerance = 0
  References2D = -> [ProjItem009]
  Rotation = 0
  ScaleType = 0
  TheoreticalExact = false
  Type = 1
  UnderTolerance = 0
  X = 24.7518
  Y = 43.405
FEATURE [TechDraw::DrawViewDimension] Dimension092
  AngleOverride = false
  Arbitrary = false
  ArbitraryTolerances = false
  EqualTolerance = true
  ExtensionAngle = 0
  FormatSpec = %.2w
  FormatSpecOverTolerance = %+.2w
  FormatSpecUnderTolerance = %+.2w
  Inverted = false
  LineAngle = 0
  LockPosition = false
  MeasureType = 1
  OverTolerance = 0
  References2D = -> [ProjItem009]
  Rotation = 0
  ScaleType = 0
  TheoreticalExact = false
  Type = 1
  UnderTolerance = 0
  X = 25.3413
  Y = 34.4599
FEATURE [TechDraw::DrawViewDimension] Dimension093
  AngleOverride = false
  Arbitrary = false
  ArbitraryTolerances = false
  EqualTolerance = true
  ExtensionAngle = 0
  FormatSpec = %.2w
  FormatSpecOverTolerance = %+.2w
  FormatSpecUnderTolerance = %+.2w
  Inverted = false
  LineAngle = 0
  LockPosition = false
  MeasureType = 1
  OverTolerance = 0
  References2D = -> [ProjItem009]
  Rotation = 0
  ScaleType = 0
  TheoreticalExact = false
  Type = 2
  UnderTolerance = 0
  X = -74.8396
  Y = 33.1325
FEATURE [TechDraw::DrawViewDimension] Dimension094
  AngleOverride = false
  Arbitrary = false
  ArbitraryTolerances = false
  EqualTolerance = true
  ExtensionAngle = 0
  FormatSpec = %.2w
  FormatSpecOverTolerance = %+.2w
  FormatSpecUnderTolerance = %+.2w
  Inverted = false
  LineAngle = 0
  LockPosition = false
  MeasureType = 1
  OverTolerance = 0
  References2D = -> [ProjItem009]
  Rotation = 0
  ScaleType = 0
  TheoreticalExact = false
  Type = 2
  UnderTolerance = 0
  X = -66.3189
  Y = 32.0863
FEATURE [TechDraw::DrawViewDimension] Dimension095
  AngleOverride = false
  Arbitrary = false
  ArbitraryTolerances = false
  EqualTolerance = true
  ExtensionAngle = 0
  FormatSpec = %.2w
  FormatSpecOverTolerance = %+.2w
  FormatSpecUnderTolerance = %+.2w
  Inverted = false
  LineAngle = 0
  LockPosition = false
  MeasureType = 1
  OverTolerance = 0
  References2D = -> [ProjItem009]
  Rotation = 0
  ScaleType = 0
  TheoreticalExact = false
  Type = 2
  UnderTolerance = 0
  X = -74.2404
  Y = -13.3775
FEATURE [TechDraw::DrawViewDimension] Dimension096
  AngleOverride = false
  Arbitrary = false
  ArbitraryTolerances = false
  EqualTolerance = true
  ExtensionAngle = 0
  FormatSpec = ⌀%.2w
  FormatSpecOverTolerance = %+.2w
  FormatSpecUnderTolerance = %+.2w
  Inverted = false
  LineAngle = 0
  LockPosition = false
  MeasureType = 1
  OverTolerance = 0
  References2D = -> [ProjItem009]
  Rotation = 0
  ScaleType = 0
  TheoreticalExact = false
  Type = 5
  UnderTolerance = 0
  X = -57.9978
  Y = 6.92635
FEATURE [TechDraw::DrawSVGTemplate] Template006
  EditableTexts = Designed_by_Name=Thomas Spielauer; FC-Date=2024-05-15; FC-SC=mm; FC-SH=2/3; FC-Title=Unshielded kicker, 40mm; Subtitle=XL30 Column Mount, Part B
  Height = 210
  Orientation = 1
  Template = <path>
  Width = 297
FEATURE [TechDraw::DrawViewPart] View002
  CoarseView = false
  Direction = (-1,0,0)
  Focus = 100
  HardHidden = false
  IsoCount = 0
  IsoHidden = false
  IsoVisible = false
  LockPosition = false
  Perspective = false
  Rotation = 0
  Scale = 2
  ScaleType = 2
  ScrubCount = 0
  SeamHidden = false
  SeamVisible = false
  SmoothHidden = false
  SmoothVisible = true
  Source = -> [Cut006]
  X = 69.3706
  XDirection = (0,0,1)
  Y = 142.315
FEATURE [TechDraw::DrawViewSection] SectionView002  label="Section002  - "
  BaseView = -> View002
  CoarseView = false
  CutSurfaceDisplay = 2
  Direction = (0,-1e-16,-1)
  FileGeomPattern = <path>
  FileHatchPattern = <path>
  Focus = 100
  FuseBeforeCut = false
  HardHidden = false
  HatchOffset = (0,0,0)
  HatchRotation = 0
  HatchScale = 1
  IsoCount = 0
  IsoHidden = false
  IsoVisible = false
  LockPosition = false
  NameGeomPattern = Diamond
  Perspective = false
  Rotation = -90
  Scale = 4
  ScaleType = 2
  ScrubCount = 0
  SeamHidden = false
  SeamVisible = false
  SectionDirection = 4
  SectionLineStretch = 1
  SectionNormal = (0,-1e-16,-1)
  SectionOrigin = (1.87,0,45.25)
  SmoothHidden = false
  SmoothVisible = true
  Source = -> [Cut006]
  TrimAfterCut = false
  UsePreviousCut = false
  X = 168.776
  XDirection = (0,-1,1e-16)
  Y = 126.942
FEATURE [TechDraw::DrawViewDimension] Dimension097
  AngleOverride = false
  Arbitrary = false
  ArbitraryTolerances = false
  EqualTolerance = true
  ExtensionAngle = 0
  FormatSpec = %.2w
  FormatSpecOverTolerance = %+.2w
  FormatSpecUnderTolerance = %+.2w
  Inverted = false
  LineAngle = 0
  LockPosition = false
  MeasureType = 1
  OverTolerance = 0
  References2D = -> [SectionView002]
  Rotation = 0
  ScaleType = 0
  TheoreticalExact = false
  Type = 2
  UnderTolerance = 0
  X = 27.1436
  Y = -5.37582
FEATURE [TechDraw::DrawViewDimension] Dimension098
  AngleOverride = false
  Arbitrary = false
  ArbitraryTolerances = false
  EqualTolerance = true
  ExtensionAngle = 0
  FormatSpec = %.2w
  FormatSpecOverTolerance = %+.2w
  FormatSpecUnderTolerance = %+.2w
  Inverted = false
  LineAngle = 0
  LockPosition = false
  MeasureType = 1
  OverTolerance = 0
  References2D = -> [SectionView002]
  Rotation = 0
  ScaleType = 0
  TheoreticalExact = false
  Type = 2
  UnderTolerance = 0
  X = 35.8994
  Y = -4.75851
FEATURE [TechDraw::DrawViewDimension] Dimension099
  AngleOverride = false
  Arbitrary = false
  ArbitraryTolerances = false
  EqualTolerance = true
  ExtensionAngle = 0
  FormatSpec = %.2w
  FormatSpecOverTolerance = %+.2w
  FormatSpecUnderTolerance = %+.2w
  Inverted = false
  LineAngle = 0
  LockPosition = false
  MeasureType = 1
  OverTolerance = 0
  References2D = -> [SectionView002]
  Rotation = 0
  ScaleType = 0
  TheoreticalExact = false
  Type = 2
  UnderTolerance = 0
  X = 44.86
  Y = -4.60418
FEATURE [TechDraw::DrawViewDimension] Dimension100
  AngleOverride = false
  Arbitrary = false
  ArbitraryTolerances = false
  EqualTolerance = true
  ExtensionAngle = 0
  FormatSpec = %.2w
  FormatSpecOverTolerance = %+.2w
  FormatSpecUnderTolerance = %+.2w
  Inverted = false
  LineAngle = 0
  LockPosition = false
  MeasureType = 1
  OverTolerance = 0
  References2D = -> [SectionView002]
  Rotation = 0
  ScaleType = 0
  TheoreticalExact = false
  Type = 1
  UnderTolerance = 0
  X = 20.9151
  Y = 57.6847
FEATURE [TechDraw::DrawViewDimension] Dimension101
  AngleOverride = false
  Arbitrary = false
  ArbitraryTolerances = false
  EqualTolerance = true
  ExtensionAngle = 0
  FormatSpec = %.2w
  FormatSpecOverTolerance = %+.2w
  FormatSpecUnderTolerance = %+.2w
  Inverted = false
  LineAngle = 0
  LockPosition = false
  MeasureType = 1
  OverTolerance = 0
  References2D = -> [SectionView002]
  Rotation = 0
  ScaleType = 0
  TheoreticalExact = false
  Type = 1
  UnderTolerance = 0
  X = 23.0081
  Y = 66.1928
FEATURE [TechDraw::DrawViewDimension] Dimension102
  AngleOverride = false
  Arbitrary = false
  ArbitraryTolerances = false
  EqualTolerance = true
  ExtensionAngle = 0
  FormatSpec = %.2w
  FormatSpecOverTolerance = %+.2w
  FormatSpecUnderTolerance = %+.2w
  Inverted = false
  LineAngle = 0
  LockPosition = false
  MeasureType = 1
  OverTolerance = 0
  References2D = -> [SectionView002]
  Rotation = 0
  ScaleType = 0
  TheoreticalExact = false
  Type = 1
  UnderTolerance = 0
  X = 22.8309
  Y = 73.1858
FEATURE [TechDraw::DrawPage] Page006  label="Page_CopperB_2"
  KeepUpdated = true
  NextBalloonIndex = 1
  ProjectionType = 0
  Template = -> Template006
  Views = -> [View002,SectionView002,Dimension097,Dimension098,Dimension099,Dimension100,Dimension101,Dimension102]
FEATURE [TechDraw::DrawSVGTemplate] Template007
  EditableTexts = Designed_by_Name=Thomas Spielauer; FC-Date=2024-05-15; FC-SC=mm; FC-SH=3/3; FC-Title=Unshielded kicker, 40mm; Subtitle=XL30 Column Mount, Part B
  Height = 210
  Orientation = 1
  Template = <path>
  Width = 297
FEATURE [TechDraw::DrawViewPart] View003
  CoarseView = false
  Direction = (-1,0,0)
  Focus = 100
  HardHidden = false
  IsoCount = 0
  IsoHidden = false
  IsoVisible = false
  LockPosition = false
  Perspective = false
  Rotation = 0
  Scale = 2
  ScaleType = 2
  ScrubCount = 0
  SeamHidden = false
  SeamVisible = false
  SmoothHidden = false
  SmoothVisible = true
  Source = -> [Cut006]
  X = 77.07
  XDirection = (0,0,1)
  Y = 148.706
FEATURE [TechDraw::DrawViewSection] SectionView003  label="Section003  - "
  BaseView = -> View003
  CoarseView = false
  CutSurfaceDisplay = 2
  Direction = (0,-1e-16,-1)
  FileGeomPattern = <path>
  FileHatchPattern = <path>
  Focus = 100
  FuseBeforeCut = false
  HardHidden = false
  HatchOffset = (0,0,0)
  HatchRotation = 0
  HatchScale = 1
  IsoCount = 0
  IsoHidden = false
  IsoVisible = false
  LockPosition = false
  NameGeomPattern = Diamond
  Perspective = false
  Rotation = -90
  Scale = 4
  ScaleType = 2
  ScrubCount = 0
  SeamHidden = false
  SeamVisible = false
  SectionDirection = 4
  SectionLineStretch = 1
  SectionNormal = (0,-1e-16,-1)
  SectionOrigin = (1.87,0,35.5)
  SmoothHidden = false
  SmoothVisible = true
  Source = -> [Cut006]
  TrimAfterCut = false
  UsePreviousCut = false
  X = 150.783
  XDirection = (0,-1,1e-16)
  Y = 129.462
FEATURE [TechDraw::DrawViewDimension] Dimension103
  AngleOverride = false
  Arbitrary = false
  ArbitraryTolerances = false
  EqualTolerance = true
  ExtensionAngle = 0
  FormatSpec = %.2w
  FormatSpecOverTolerance = %+.2w
  FormatSpecUnderTolerance = %+.2w
  Inverted = false
  LineAngle = 0
  LockPosition = false
  MeasureType = 1
  OverTolerance = 0
  References2D = -> [SectionView003]
  Rotation = 0
  ScaleType = 0
  TheoreticalExact = false
  Type = 2
  UnderTolerance = 0
  X = 21.224
  Y = 33.4785
FEATURE [TechDraw::DrawViewDimension] Dimension104
  AngleOverride = false
  Arbitrary = false
  ArbitraryTolerances = false
  EqualTolerance = true
  ExtensionAngle = 0
  FormatSpec = %.2w
  FormatSpecOverTolerance = %+.2w
  FormatSpecUnderTolerance = %+.2w
  Inverted = false
  LineAngle = 0
  LockPosition = false
  MeasureType = 1
  OverTolerance = 0
  References2D = -> [SectionView003]
  Rotation = 0
  ScaleType = 0
  TheoreticalExact = false
  Type = 1
  UnderTolerance = 0
  X = 0.326165
  Y = 62.5681
FEATURE [TechDraw::DrawPage] Page007  label="Page_CopperB_3"
  KeepUpdated = true
  NextBalloonIndex = 1
  ProjectionType = 0
  Template = -> Template007
  Views = -> [View003,SectionView003,Dimension103,Dimension104]
FEATURE [TechDraw::DrawViewAnnotation] Annotation002
  Font = osifont
  LineSpace = 100
  LockPosition = false
  MaxWidth = -1
  Rotation = 0
  ScaleType = 0
  Text = Material: Copper
  TextSize = 5
  TextStyle = 0
  X = 37.7194
  Y = 21.0052
FEATURE [TechDraw::DrawPage] Page002  label="Page_CopperA_1"
  KeepUpdated = true
  NextBalloonIndex = 1
  ProjectionType = 0
  Template = -> Template002
  Views = -> [ProjGroup002,Dimension038,Dimension039,Dimension040,Dimension041,Dimension042,Dimension043,Dimension044,Dimension045,Dimension046,Dimension047,Dimension048,Dimension049,Dimension050,Dimension051,Dimension052,Dimension053,Dimension054,Dimension055,Dimension056,Dimension057,Dimension058,Dimension059,Dimension060,Dimension061,Dimension062,Dimension063,Annotation002]
FEATURE [TechDraw::DrawViewAnnotation] Annotation003
  Font = osifont
  LineSpace = 100
  LockPosition = false
  MaxWidth = -1
  Rotation = 0
  ScaleType = 0
  Text = Material: Copper
  TextSize = 5
  TextStyle = 0
  X = 36.6927
  Y = 21.3994
FEATURE [TechDraw::DrawPage] Page005  label="Page_CopperB_1"
  KeepUpdated = true
  NextBalloonIndex = 1
  ProjectionType = 0
  Template = -> Template005
  Views = -> [ProjGroup003,Dimension073,Dimension074,Dimension075,Dimension076,Dimension077,Dimension078,Dimension079,Dimension080,Dimension081,Dimension082,Dimension083,Dimension084,Dimension085,Dimension086,Dimension087,Dimension088,Dimension089,Dimension090,Dimension091,Dimension092,Dimension093,Dimension094,Dimension095,Dimension096,Annotation003]
FEATURE [Part::Feature] Cut008_solid  label="CopperA (Solid)"
  shape: bbox 3.25 x 24 x 40 mm, 40 faces (baked)
FEATURE [Part::Feature] Cut006_solid  label="CopperB (Solid)"
  shape: bbox 3.25 x 24 x 40 mm, 38 faces (baked)
FEATURE [Part::Feature] Cut009_solid  label="Holder (Solid)"
  shape: bbox 8 x 42 x 20 mm, 38 faces (baked)
FEATURE [Part::Feature] Cut010_solid  label="GNDPlate (Solid)"
  shape: bbox 44 x 42 x 1 mm, 11 faces (baked)
FEATURE [Part::Feature] Cut008_solid001  label="CopperA (Solid)001"
  shape: bbox 3.25 x 24 x 40 mm, 40 faces (baked)
FEATURE [Part::Feature] Cut006_solid001  label="CopperB (Solid)001"
  shape: bbox 3.25 x 24 x 40 mm, 38 faces (baked)
FEATURE [Part::Feature] Cut009_solid001  label="Holder (Solid)001"
  shape: bbox 8 x 42 x 20 mm, 38 faces (baked)
FEATURE [Part::Feature] Cut010_solid001  label="GNDPlate (Solid)001"
  shape: bbox 44 x 42 x 1 mm, 11 faces (baked)
FEATURE [Part::Compound] Compound  label="KickerAssembly"
  Links = -> [Cut008_solid001,Cut006_solid001,Cut009_solid001,Cut010_solid001]
note: 16 file-system paths scrubbed to <path> (originals preserved in the JSON sidecar)

RESOLVED EXTERNAL PARTS (link-assembly join: the EXTERNAL_REF files above that resolve inside this repo's crawl, each included once):
---- part ../../Spacers/Macor/4mmOD_M2_5.5mm.FCStd = doc fcstd_6bfad48120a3 ----
FCSTD DOCUMENT  (FreeCAD 0.22R0.21.2)
Label: 4mmOD_M2_5.5mm
License: All rights reserved
LicenseURL: http://en.wikipedia.org/wiki/All_rights_reserved
objects: Part::Cylinder×3, Part::MultiFuse×1, Part::Cut×1
note: 5 computed .brp shape members not serialized (recipe doc carries the construction recipe); baked Part::Feature solids carry a one-line shape summary decoded from their .brp

FEATURE [Part::Cylinder] Cylinder
  Angle = 360
  AttacherType = Attacher::AttachEngine3D
  FirstAngle = 0
  Height = 3.5
  Radius = 2.5
  SecondAngle = 0
FEATURE [Part::Cylinder] Cylinder001
  Angle = 360
  AttacherType = Attacher::AttachEngine3D
  FirstAngle = 0
  Height = 5.2
  Radius = 2
  SecondAngle = 0
FEATURE [Part::MultiFuse] Fusion
  Shapes = -> [Cylinder001,Cylinder]
FEATURE [Part::Cylinder] Cylinder002
  Angle = 360
  AttacherType = Attacher::AttachEngine3D
  FirstAngle = 0
  Height = 10
  Radius = 0.9
  SecondAngle = 0
FEATURE [Part::Cut] Cut  label="Markor4mmOD_M2"
  Base = -> Fusion
  Tool = -> Cylinder002
---- part XL30ColumnAttachmentRing_PCBKicker01.FCStd = doc fcstd_5df1f01fb415 ----
FCSTD DOCUMENT  (FreeCAD 0.20R)
Label: XL30ColumnAttachmentRing_PCBKicker01
License: All rights reserved
LicenseURL: http://en.wikipedia.org/wiki/All_rights_reserved
objects: Part::Cylinder×30, TechDraw::DrawViewDimension×23, Part::Compound×20, Part::Cut×7, TechDraw::DrawProjGroupItem×4, Part::Box×3, Part::MultiFuse×2, TechDraw::DrawSVGTemplate×2, TechDraw::DrawProjGroup×2, TechDraw::DrawPage×2, Part::MultiCommon×1, TechDraw::DrawViewSection×1, TechDraw::DrawViewAnnotation×1
note: 63 computed .brp shape members not serialized (recipe doc carries the construction recipe); baked Part::Feature solids carry a one-line shape summary decoded from their .brp
EXTERNAL_REF file=XL30ColumnAttachmentRing01.FCStd obj=Spreadsheet

FEATURE [Part::Cylinder] Cylinder
  Angle = 360
  AttacherType = Attacher::AttachEngine3D
  FirstAngle = 0
  Height = 5
  Radius = 57.66
  SecondAngle = 0
  expr: Height = <<XL30ColumnAttachmentRing01>>#<<AttachmentRing01>>.ring_thickness
  expr: Radius = <<XL30ColumnAttachmentRing01>>#<<AttachmentRing01>>.ring_od / 2
FEATURE [Part::Cylinder] Cylinder001
  Angle = 360
  AttacherType = Attacher::AttachEngine3D
  FirstAngle = 0
  Height = 5
  Radius = 50
  SecondAngle = 0
  expr: Height = <<XL30ColumnAttachmentRing01>>#<<AttachmentRing01>>.ring_thickness
  expr: Radius = <<XL30ColumnAttachmentRing01>>#<<AttachmentRing01>>.ring_id / 2
FEATURE [Part::Cut] Cut
  Base = -> Cylinder
  Tool = -> Cylinder001
FEATURE [Part::Cylinder] Cylinder002
  Angle = 360
  AttacherType = Attacher::AttachEngine3D
  FirstAngle = 0
  Height = 5
  Placement = pos=(53.83,0,0) rot=(0,0,1;0rad)
  Radius = 2.15
  SecondAngle = 0
  expr: .Placement.Base.x = (<<XL30ColumnAttachmentRing01>>#<<AttachmentRing01>>.ring_od + <<XL30ColumnAttachmentRing01>>#<<AttachmentRing01>>.ring_id) / 4
  expr: Height = <<XL30ColumnAttachmentRing01>>#<<AttachmentRing01>>.ring_thickness
FEATURE [Part::Compound] Compound
  Links = -> [Cylinder002]
FEATURE [Part::Cylinder] Cylinder003
  Angle = 360
  AttacherType = Attacher::AttachEngine3D
  FirstAngle = 0
  Height = 5
  Placement = pos=(53.83,0,0) rot=(0,0,1;0rad)
  Radius = 2.15
  SecondAngle = 0
  expr: .Placement.Base.x = (<<XL30ColumnAttachmentRing01>>#<<AttachmentRing01>>.ring_od + <<XL30ColumnAttachmentRing01>>#<<AttachmentRing01>>.ring_id) / 4
  expr: Height = <<XL30ColumnAttachmentRing01>>#<<AttachmentRing01>>.ring_thickness
FEATURE [Part::Compound] Compound001
  Links = -> [Cylinder003]
  Placement = pos=(0,0,0) rot=(0,0,1;0.785398rad)
FEATURE [Part::Cylinder] Cylinder004
  Angle = 360
  AttacherType = Attacher::AttachEngine3D
  FirstAngle = 0
  Height = 5
  Placement = pos=(53.83,0,0) rot=(0,0,1;0rad)
  Radius = 2.15
  SecondAngle = 0
  expr: .Placement.Base.x = (<<XL30ColumnAttachmentRing01>>#<<AttachmentRing01>>.ring_od + <<XL30ColumnAttachmentRing01>>#<<AttachmentRing01>>.ring_id) / 4
  expr: Height = <<XL30ColumnAttachmentRing01>>#<<AttachmentRing01>>.ring_thickness
FEATURE [Part::Compound] Compound002
  Links = -> [Cylinder004]
  Placement = pos=(0,0,0) rot=(0,0,1;1.5708rad)
FEATURE [Part::Cylinder] Cylinder005
  Angle = 360
  AttacherType = Attacher::AttachEngine3D
  FirstAngle = 0
  Height = 5
  Placement = pos=(53.83,0,0) rot=(0,0,1;0rad)
  Radius = 2.15
  SecondAngle = 0
  expr: .Placement.Base.x = (<<XL30ColumnAttachmentRing01>>#<<AttachmentRing01>>.ring_od + <<XL30ColumnAttachmentRing01>>#<<AttachmentRing01>>.ring_id) / 4
  expr: Height = <<XL30ColumnAttachmentRing01>>#<<AttachmentRing01>>.ring_thickness
FEATURE [Part::Compound] Compound003
  Links = -> [Cylinder005]
  Placement = pos=(0,0,0) rot=(0,0,1;2.35619rad)
FEATURE [Part::Cylinder] Cylinder006
  Angle = 360
  AttacherType = Attacher::AttachEngine3D
  FirstAngle = 0
  Height = 5
  Placement = pos=(53.83,0,0) rot=(0,0,1;0rad)
  Radius = 2.15
  SecondAngle = 0
  expr: .Placement.Base.x = (<<XL30ColumnAttachmentRing01>>#<<AttachmentRing01>>.ring_od + <<XL30ColumnAttachmentRing01>>#<<AttachmentRing01>>.ring_id) / 4
  expr: Height = <<XL30ColumnAttachmentRing01>>#<<AttachmentRing01>>.ring_thickness
FEATURE [Part::Compound] Compound004
  Links = -> [Cylinder006]
  Placement = pos=(0,0,0) rot=(0,0,1;3.14159rad)
FEATURE [Part::Cylinder] Cylinder007
  Angle = 360
  AttacherType = Attacher::AttachEngine3D
  FirstAngle = 0
  Height = 5
  Placement = pos=(53.83,0,0) rot=(0,0,1;0rad)
  Radius = 2.15
  SecondAngle = 0
  expr: .Placement.Base.x = (<<XL30ColumnAttachmentRing01>>#<<AttachmentRing01>>.ring_od + <<XL30ColumnAttachmentRing01>>#<<AttachmentRing01>>.ring_id) / 4
  expr: Height = <<XL30ColumnAttachmentRing01>>#<<AttachmentRing01>>.ring_thickness
FEATURE [Part::Compound] Compound005
  Links = -> [Cylinder007]
  Placement = pos=(0,0,0) rot=(0,0,1;3.92699rad)
FEATURE [Part::Cylinder] Cylinder008
  Angle = 360
  AttacherType = Attacher::AttachEngine3D
  FirstAngle = 0
  Height = 5
  Placement = pos=(53.83,0,0) rot=(0,0,1;0rad)
  Radius = 2.15
  SecondAngle = 0
  expr: .Placement.Base.x = (<<XL30ColumnAttachmentRing01>>#<<AttachmentRing01>>.ring_od + <<XL30ColumnAttachmentRing01>>#<<AttachmentRing01>>.ring_id) / 4
  expr: Height = <<XL30ColumnAttachmentRing01>>#<<AttachmentRing01>>.ring_thickness
FEATURE [Part::Compound] Compound006
  Links = -> [Cylinder008]
  Placement = pos=(0,0,0) rot=(0,0,1;4.71239rad)
FEATURE [Part::Cylinder] Cylinder009
  Angle = 360
  AttacherType = Attacher::AttachEngine3D
  FirstAngle = 0
  Height = 5
  Placement = pos=(53.83,0,0) rot=(0,0,1;0rad)
  Radius = 2.15
  SecondAngle = 0
  expr: .Placement.Base.x = (<<XL30ColumnAttachmentRing01>>#<<AttachmentRing01>>.ring_od + <<XL30ColumnAttachmentRing01>>#<<AttachmentRing01>>.ring_id) / 4
  expr: Height = <<XL30ColumnAttachmentRing01>>#<<AttachmentRing01>>.ring_thickness
FEATURE [Part::Compound] Compound007
  Links = -> [Cylinder009]
  Placement = pos=(0,0,0) rot=(0,0,1;5.49779rad)
FEATURE [Part::Compound] Compound008  label="M4ThroughHoles"
  Links = -> [Compound,Compound001,Compound002,Compound003,Compound004,Compound005,Compound006,Compound007]
FEATURE [Part::Cut] Cut001  label="OuterBaseRing"
  Base = -> Cut
  Tool = -> Compound008
FEATURE [Part::Cylinder] Cylinder010
  Angle = 360
  AttacherType = Attacher::AttachEngine3D
  FirstAngle = 0
  Height = 5
  Radius = 57.66
  SecondAngle = 0
  expr: Height = <<XL30ColumnAttachmentRing01>>#<<AttachmentRing01>>.ring_thickness
  expr: Radius = <<XL30ColumnAttachmentRing01>>#<<AttachmentRing01>>.ring_od / 2
FEATURE [Part::Cylinder] Cylinder011
  Angle = 360
  AttacherType = Attacher::AttachEngine3D
  FirstAngle = 0
  Height = 5
  Radius = 50
  SecondAngle = 0
  expr: Height = <<XL30ColumnAttachmentRing01>>#<<AttachmentRing01>>.ring_thickness
  expr: Radius = <<XL30ColumnAttachmentRing01>>#<<AttachmentRing01>>.ring_id / 2
FEATURE [Part::Cut] Cut002
  Base = -> Cylinder010
  Tool = -> Cylinder011
FEATURE [Part::Cylinder] Cylinder012
  Angle = 360
  AttacherType = Attacher::AttachEngine3D
  FirstAngle = 0
  Height = 5
  Placement = pos=(53.83,0,0) rot=(0,0,1;0rad)
  Radius = 2.15
  SecondAngle = 0
  expr: .Placement.Base.x = (<<XL30ColumnAttachmentRing01>>#<<AttachmentRing01>>.ring_od + <<XL30ColumnAttachmentRing01>>#<<AttachmentRing01>>.ring_id) / 4
  expr: Height = <<XL30ColumnAttachmentRing01>>#<<AttachmentRing01>>.ring_thickness
FEATURE [Part::Compound] Compound009
  Links = -> [Cylinder012]
FEATURE [Part::Cylinder] Cylinder013
  Angle = 360
  AttacherType = Attacher::AttachEngine3D
  FirstAngle = 0
  Height = 5
  Placement = pos=(53.83,0,0) rot=(0,0,1;0rad)
  Radius = 2.15
  SecondAngle = 0
  expr: .Placement.Base.x = (<<XL30ColumnAttachmentRing01>>#<<AttachmentRing01>>.ring_od + <<XL30ColumnAttachmentRing01>>#<<AttachmentRing01>>.ring_id) / 4
  expr: Height = <<XL30ColumnAttachmentRing01>>#<<AttachmentRing01>>.ring_thickness
FEATURE [Part::Compound] Compound010
  Links = -> [Cylinder013]
  Placement = pos=(0,0,0) rot=(0,0,1;0.785398rad)
FEATURE [Part::Cylinder] Cylinder014
  Angle = 360
  AttacherType = Attacher::AttachEngine3D
  FirstAngle = 0
  Height = 5
  Placement = pos=(53.83,0,0) rot=(0,0,1;0rad)
  Radius = 2.15
  SecondAngle = 0
  expr: .Placement.Base.x = (<<XL30ColumnAttachmentRing01>>#<<AttachmentRing01>>.ring_od + <<XL30ColumnAttachmentRing01>>#<<AttachmentRing01>>.ring_id) / 4
  expr: Height = <<XL30ColumnAttachmentRing01>>#<<AttachmentRing01>>.ring_thickness
FEATURE [Part::Compound] Compound011
  Links = -> [Cylinder014]
  Placement = pos=(0,0,0) rot=(0,0,1;1.5708rad)
FEATURE [Part::Cylinder] Cylinder015
  Angle = 360
  AttacherType = Attacher::AttachEngine3D
  FirstAngle = 0
  Height = 5
  Placement = pos=(53.83,0,0) rot=(0,0,1;0rad)
  Radius = 2.15
  SecondAngle = 0
  expr: .Placement.Base.x = (<<XL30ColumnAttachmentRing01>>#<<AttachmentRing01>>.ring_od + <<XL30ColumnAttachmentRing01>>#<<AttachmentRing01>>.ring_id) / 4
  expr: Height = <<XL30ColumnAttachmentRing01>>#<<AttachmentRing01>>.ring_thickness
FEATURE [Part::Compound] Compound012
  Links = -> [Cylinder015]
  Placement = pos=(0,0,0) rot=(0,0,1;2.35619rad)
FEATURE [Part::Cylinder] Cylinder016
  Angle = 360
  AttacherType = Attacher::AttachEngine3D
  FirstAngle = 0
  Height = 5
  Placement = pos=(53.83,0,0) rot=(0,0,1;0rad)
  Radius = 2.15
  SecondAngle = 0
  expr: .Placement.Base.x = (<<XL30ColumnAttachmentRing01>>#<<AttachmentRing01>>.ring_od + <<XL30ColumnAttachmentRing01>>#<<AttachmentRing01>>.ring_id) / 4
  expr: Height = <<XL30ColumnAttachmentRing01>>#<<AttachmentRing01>>.ring_thickness
FEATURE [Part::Compound] Compound013
  Links = -> [Cylinder016]
  Placement = pos=(0,0,0) rot=(0,0,1;3.14159rad)
FEATURE [Part::Cylinder] Cylinder017
  Angle = 360
  AttacherType = Attacher::AttachEngine3D
  FirstAngle = 0
  Height = 5
  Placement = pos=(53.83,0,0) rot=(0,0,1;0rad)
  Radius = 2.15
  SecondAngle = 0
  expr: .Placement.Base.x = (<<XL30ColumnAttachmentRing01>>#<<AttachmentRing01>>.ring_od + <<XL30ColumnAttachmentRing01>>#<<AttachmentRing01>>.ring_id) / 4
  expr: Height = <<XL30ColumnAttachmentRing01>>#<<AttachmentRing01>>.ring_thickness
FEATURE [Part::Compound] Compound014
  Links = -> [Cylinder017]
  Placement = pos=(0,0,0) rot=(0,0,1;3.92699rad)
FEATURE [Part::Cylinder] Cylinder018
  Angle = 360
  AttacherType = Attacher::AttachEngine3D
  FirstAngle = 0
  Height = 5
  Placement = pos=(53.83,0,0) rot=(0,0,1;0rad)
  Radius = 2.15
  SecondAngle = 0
  expr: .Placement.Base.x = (<<XL30ColumnAttachmentRing01>>#<<AttachmentRing01>>.ring_od + <<XL30ColumnAttachmentRing01>>#<<AttachmentRing01>>.ring_id) / 4
  expr: Height = <<XL30ColumnAttachmentRing01>>#<<AttachmentRing01>>.ring_thickness
FEATURE [Part::Compound] Compound015
  Links = -> [Cylinder018]
  Placement = pos=(0,0,0) rot=(0,0,-1;1.5708rad)
FEATURE [Part::Cylinder] Cylinder019
  Angle = 360
  AttacherType = Attacher::AttachEngine3D
  FirstAngle = 0
  Height = 5
  Placement = pos=(53.83,0,0) rot=(0,0,1;0rad)
  Radius = 2.15
  SecondAngle = 0
  expr: .Placement.Base.x = (<<XL30ColumnAttachmentRing01>>#<<AttachmentRing01>>.ring_od + <<XL30ColumnAttachmentRing01>>#<<AttachmentRing01>>.ring_id) / 4
  expr: Height = <<XL30ColumnAttachmentRing01>>#<<AttachmentRing01>>.ring_thickness
FEATURE [Part::Compound] Compound016
  Links = -> [Cylinder019]
  Placement = pos=(0,0,0) rot=(0,0,-1;0.785398rad)
FEATURE [Part::Compound] Compound017  label="M4ThroughHoles001"
  Links = -> [Compound009,Compound010,Compound011,Compound012,Compound013,Compound014,Compound015,Compound016]
FEATURE [Part::Cut] Cut003  label="Ring01"
  Base = -> Cut002
  Tool = -> Compound017
FEATURE [Part::Box] Box  label="Cube"
  AttacherType = Attacher::AttachEngine3D
  Height = 20
  Length = 40
  Width = 42
FEATURE [Part::Cylinder] Cylinder020
  Angle = 360
  AttacherType = Attacher::AttachEngine3D
  FirstAngle = 0
  Height = 20
  Placement = pos=(10,21,0) rot=(0,0,1;0rad)
  Radius = 2
  SecondAngle = 0
FEATURE [Part::Cut] Cut004
  Base = -> Box
  Tool = -> Cylinder020
FEATURE [Part::Cylinder] Cylinder021
  Angle = 360
  AttacherType = Attacher::AttachEngine3D
  FirstAngle = 0
  Height = 20
  Placement = pos=(2.5,2.5,0) rot=(0,0,1;0rad)
  Radius = 1.3
  SecondAngle = 0
FEATURE [Part::Cylinder] Cylinder022
  Angle = 360
  AttacherType = Attacher::AttachEngine3D
  FirstAngle = 0
  Height = 20
  Placement = pos=(37.5,2.5,0) rot=(0,0,1;0rad)
  Radius = 1.3
  SecondAngle = 0
FEATURE [Part::Cylinder] Cylinder023
  Angle = 360
  AttacherType = Attacher::AttachEngine3D
  FirstAngle = 0
  Height = 20
  Placement = pos=(2.5,39.5,0) rot=(0,0,1;0rad)
  Radius = 1.3
  SecondAngle = 0
FEATURE [Part::Cylinder] Cylinder024
  Angle = 360
  AttacherType = Attacher::AttachEngine3D
  FirstAngle = 0
  Height = 20
  Placement = pos=(37.5,39.5,0) rot=(0,0,1;0rad)
  Radius = 1.3
  SecondAngle = 0
FEATURE [Part::Compound] Compound018
  Links = -> [Cylinder021,Cylinder022,Cylinder023,Cylinder024]
FEATURE [Part::Cut] Cut005  label="PCBStackTemplate"
  Base = -> Cut004
  Placement = pos=(-10,-21,5) rot=(0,0,1;0rad)
  Tool = -> Compound018
FEATURE [Part::Cylinder] Cylinder025
  Angle = 360
  AttacherType = Attacher::AttachEngine3D
  FirstAngle = 0
  Height = 20
  Placement = pos=(2.5,2.5,0) rot=(0,0,1;0rad)
  Radius = 1.3
  SecondAngle = 0
FEATURE [Part::Cylinder] Cylinder026
  Angle = 360
  AttacherType = Attacher::AttachEngine3D
  FirstAngle = 0
  Height = 20
  Placement = pos=(37.5,2.5,0) rot=(0,0,1;0rad)
  Radius = 1.3
  SecondAngle = 0
FEATURE [Part::Cylinder] Cylinder027
  Angle = 360
  AttacherType = Attacher::AttachEngine3D
  FirstAngle = 0
  Height = 20
  Placement = pos=(2.5,39.5,0) rot=(0,0,1;0rad)
  Radius = 1.3
  SecondAngle = 0
FEATURE [Part::Cylinder] Cylinder028
  Angle = 360
  AttacherType = Attacher::AttachEngine3D
  FirstAngle = 0
  Height = 20
  Placement = pos=(37.5,39.5,0) rot=(0,0,1;0rad)
  Radius = 1.3
  SecondAngle = 0
FEATURE [Part::Compound] Compound019  label="M3Mountholes"
  Links = -> [Cylinder025,Cylinder026,Cylinder027,Cylinder028]
  Placement = pos=(-10,-21,0) rot=(0,0,1;0rad)
FEATURE [Part::Box] Box001  label="Cube001"
  AttacherType = Attacher::AttachEngine3D
  Height = 3
  Length = 115.32
  Placement = pos=(-57.66,-21,2) rot=(0,0,1;0rad)
  Width = 5
  expr: .Placement.Base.x = -<<XL30ColumnAttachmentRing01>>#<<AttachmentRing01>>.ring_od / 2
  expr: .Placement.Base.z = <<XL30ColumnAttachmentRing01>>#<<AttachmentRing01>>.ring_thickness - 3
  expr: Length = <<XL30ColumnAttachmentRing01>>#<<AttachmentRing01>>.ring_od
FEATURE [Part::Box] Box002  label="Cube002"
  AttacherType = Attacher::AttachEngine3D
  Height = 3
  Length = 115.32
  Placement = pos=(-57.66,16,2) rot=(0,0,1;0rad)
  Width = 5
  expr: .Placement.Base.x = -<<XL30ColumnAttachmentRing01>>#<<AttachmentRing01>>.ring_od / 2
  expr: .Placement.Base.z = <<XL30ColumnAttachmentRing01>>#<<AttachmentRing01>>.ring_thickness - 3
  expr: Length = <<XL30ColumnAttachmentRing01>>#<<AttachmentRing01>>.ring_od
FEATURE [Part::MultiFuse] Fusion
  Shapes = -> [Box001,Box002]
FEATURE [Part::Cylinder] Cylinder029
  Angle = 360
  AttacherType = Attacher::AttachEngine3D
  FirstAngle = 0
  Height = 5
  Radius = 57.66
  SecondAngle = 0
  expr: Height = <<XL30ColumnAttachmentRing01>>#<<AttachmentRing01>>.ring_thickness
  expr: Radius = <<XL30ColumnAttachmentRing01>>#<<AttachmentRing01>>.ring_od / 2
FEATURE [Part::MultiCommon] Common
  Shapes = -> [Fusion,Cylinder029]
FEATURE [Part::Cut] Cut006
  Base = -> Common
  Tool = -> Compound019
FEATURE [Part::MultiFuse] Fusion001  label="Stackmountring01"
  Shapes = -> [Cut003,Cut006]
FEATURE [TechDraw::DrawSVGTemplate] Template
  EditableTexts = Designed_by_Name=Thomas Spielauer; FC-Date=2023-11-15; FC-SC=mm; FC-SH=1/1; FC-Title=XL30 column cage: PCB mount; Subtitle=Compatible with XL30 column attachment ring
  Height = 210
  Orientation = 1
  Width = 297
FEATURE [TechDraw::DrawProjGroupItem] ProjItem  label="Front"
  CoarseView = false
  Direction = (0,0,1)
  Focus = 100
  HardHidden = false
  IsoCount = 0
  IsoHidden = false
  IsoVisible = false
  LockPosition = true
  Perspective = false
  Rotation = 0
  RotationVector = (1,0,0)
  ScaleType = 2
  SeamHidden = false
  SeamVisible = true
  SmoothHidden = false
  SmoothVisible = true
  Source = -> [Fusion001]
  Type = 0
  X = 0
  XDirection = (1,0,0)
  Y = 0
FEATURE [TechDraw::DrawProjGroupItem] ProjItem002  label="Top"
  CoarseView = false
  Direction = (0,1,0)
  Focus = 100
  HardHidden = false
  IsoCount = 0
  IsoHidden = false
  IsoVisible = false
  LockPosition = false
  Perspective = false
  Rotation = 0
  RotationVector = (1,0,0)
  ScaleType = 2
  SeamHidden = false
  SeamVisible = true
  SmoothHidden = false
  SmoothVisible = true
  Source = -> [Fusion001]
  Type = 4
  X = 0
  XDirection = (1,0,0)
  Y = -130.32
FEATURE [TechDraw::DrawProjGroup] ProjGroup
  Anchor = -> ProjItem
  AutoDistribute = true
  LockPosition = false
  ProjectionType = 0
  Rotation = 0
  ScaleType = 0
  Source = -> [Fusion001]
  Views = -> [ProjItem,ProjItem002]
  X = 77.9531
  Y = 128.789
  spacingX = 15
  spacingY = 15
FEATURE [TechDraw::DrawViewSection] SectionView  label="Section  - "
  BaseView = -> ProjItem
  CoarseView = false
  CutSurfaceDisplay = 2
  Direction = (-1,0,0)
  FileGeomPattern = <path>
  FileHatchPattern = <path>
  Focus = 100
  FuseBeforeCut = false
  HardHidden = false
  HatchScale = 1
  IsoCount = 0
  IsoHidden = false
  IsoVisible = false
  LockPosition = false
  NameGeomPattern = Diamond
  Perspective = false
  Rotation = 0
  ScaleType = 2
  SeamHidden = false
  SeamVisible = true
  SectionDirection = 0
  SectionNormal = (-1,0,0)
  SectionOrigin = (0,0,2.5)
  SmoothHidden = false
  SmoothVisible = true
  Source = -> [Fusion001]
  X = 175.93
  XDirection = (0,0,1)
  Y = 127.772
FEATURE [TechDraw::DrawViewDimension] Dimension
  AngleOverride = false
  Arbitrary = false
  ArbitraryTolerances = false
  EqualTolerance = true
  ExtensionAngle = 0
  FormatSpec = ⌀%.2w
  FormatSpecOverTolerance = %+.2w
  FormatSpecUnderTolerance = %+.2w
  Inverted = false
  LineAngle = 0
  LockPosition = false
  MeasureType = 1
  OverTolerance = 0
  References2D = -> [ProjItem]
  Rotation = 0
  ScaleType = 0
  TheoreticalExact = false
  Type = 5
  UnderTolerance = 0
  X = 61.5234
  Y = 45.459
FEATURE [TechDraw::DrawViewDimension] Dimension001
  AngleOverride = false
  Arbitrary = false
  ArbitraryTolerances = false
  EqualTolerance = true
  ExtensionAngle = 0
  FormatSpec = ⌀%.2w
  FormatSpecOverTolerance = %+.2w
  FormatSpecUnderTolerance = %+.2w
  Inverted = false
  LineAngle = 0
  LockPosition = false
  MeasureType = 1
  OverTolerance = 0
  References2D = -> [ProjItem]
  Rotation = 0
  ScaleType = 0
  TheoreticalExact = false
  Type = 5
  UnderTolerance = 0
  X = 66.6504
  Y = 36.5723
FEATURE [TechDraw::DrawViewDimension] Dimension002
  AngleOverride = false
  Arbitrary = false
  ArbitraryTolerances = false
  EqualTolerance = true
  ExtensionAngle = 0
  FormatSpec = ⌀%.2w (8x)
  FormatSpecOverTolerance = %+.2w
  FormatSpecUnderTolerance = %+.2w
  Inverted = false
  LineAngle = 0
  LockPosition = false
  MeasureType = 1
  OverTolerance = 0
  References2D = -> [ProjItem]
  Rotation = 0
  ScaleType = 0
  TheoreticalExact = false
  Type = 5
  UnderTolerance = 0
  X = 54.0039
  Y = 54.0039
FEATURE [TechDraw::DrawViewDimension] Dimension003
  AngleOverride = false
  Arbitrary = false
  ArbitraryTolerances = false
  EqualTolerance = true
  ExtensionAngle = 0
  FormatSpec = ⌀%.2w (4x M3)
  FormatSpecOverTolerance = %+.2w
  FormatSpecUnderTolerance = %+.2w
  Inverted = false
  LineAngle = 0
  LockPosition = false
  MeasureType = 1
  OverTolerance = 0
  References2D = -> [ProjItem]
  Rotation = 0
  ScaleType = 0
  TheoreticalExact = false
  Type = 5
  UnderTolerance = 0
  X = -25.2791
  Y = 6.47025
FEATURE [TechDraw::DrawViewDimension] Dimension004
  AngleOverride = false
  Arbitrary = false
  ArbitraryTolerances = false
  EqualTolerance = true
  ExtensionAngle = 0
  FormatSpec = ⌀%.2w
  FormatSpecOverTolerance = %+.2w
  FormatSpecUnderTolerance = %+.2w
  Inverted = false
  LineAngle = 0
  LockPosition = false
  MeasureType = 1
  OverTolerance = 0
  References2D = -> [ProjItem]
  Rotation = 0
  ScaleType = 0
  TheoreticalExact = false
  Type = 5
  UnderTolerance = 0
  X = 70.0684
  Y = 28.1982
FEATURE [TechDraw::DrawViewDimension] Dimension005
  AngleOverride = false
  Arbitrary = false
  ArbitraryTolerances = false
  EqualTolerance = true
  ExtensionAngle = 0
  FormatSpec = %.2w
  FormatSpecOverTolerance = %+.2w
  FormatSpecUnderTolerance = %+.2w
  Inverted = false
  LineAngle = 0
  LockPosition = false
  MeasureType = 1
  OverTolerance = 0
  References2D = -> [ProjItem]
  Rotation = 0
  ScaleType = 0
  TheoreticalExact = false
  Type = 6
  UnderTolerance = 0
  X = -32.2741
  Y = 59.9027
FEATURE [TechDraw::DrawViewDimension] Dimension006
  AngleOverride = false
  Arbitrary = false
  ArbitraryTolerances = false
  EqualTolerance = true
  ExtensionAngle = 0
  FormatSpec = %.2w
  FormatSpecOverTolerance = %+.2w
  FormatSpecUnderTolerance = %+.2w
  Inverted = false
  LineAngle = 0
  LockPosition = false
  MeasureType = 1
  OverTolerance = 0
  References2D = -> [ProjItem]
  Rotation = 0
  ScaleType = 0
  TheoreticalExact = false
  Type = 2
  UnderTolerance = 0
  X = 31.0643
  Y = -6.39286
FEATURE [TechDraw::DrawViewDimension] Dimension007
  AngleOverride = false
  Arbitrary = false
  ArbitraryTolerances = false
  EqualTolerance = true
  ExtensionAngle = 0
  FormatSpec = %.2w
  FormatSpecOverTolerance = %+.2w
  FormatSpecUnderTolerance = %+.2w
  Inverted = false
  LineAngle = 0
  LockPosition = false
  MeasureType = 1
  OverTolerance = 0
  References2D = -> [ProjItem]
  Rotation = 0
  ScaleType = 0
  TheoreticalExact = false
  Type = 2
  UnderTolerance = 0
  X = 31.3208
  Y = 10.3055
FEATURE [TechDraw::DrawViewDimension] Dimension008
  AngleOverride = false
  Arbitrary = false
  ArbitraryTolerances = false
  EqualTolerance = true
  ExtensionAngle = 0
  FormatSpec = %.2w
  FormatSpecOverTolerance = %+.2w
  FormatSpecUnderTolerance = %+.2w
  Inverted = false
  LineAngle = 0
  LockPosition = false
  MeasureType = 1
  OverTolerance = 0
  References2D = -> [ProjItem]
  Rotation = 0
  ScaleType = 0
  TheoreticalExact = false
  Type = 1
  UnderTolerance = 0
  X = -4.11113
  Y = 33.5088
FEATURE [TechDraw::DrawViewDimension] Dimension009
  AngleOverride = false
  Arbitrary = false
  ArbitraryTolerances = false
  EqualTolerance = true
  ExtensionAngle = 0
  FormatSpec = %.2w
  FormatSpecOverTolerance = %+.2w
  FormatSpecUnderTolerance = %+.2w
  Inverted = false
  LineAngle = 0
  LockPosition = false
  MeasureType = 1
  OverTolerance = 0
  References2D = -> [ProjItem]
  Rotation = 0
  ScaleType = 0
  TheoreticalExact = false
  Type = 1
  UnderTolerance = 0
  X = 14.1111
  Y = 36.2173
FEATURE [TechDraw::DrawViewDimension] Dimension010
  AngleOverride = false
  Arbitrary = false
  ArbitraryTolerances = false
  EqualTolerance = true
  ExtensionAngle = 0
  FormatSpec = %.2w
  FormatSpecOverTolerance = %+.2w
  FormatSpecUnderTolerance = %+.2w
  Inverted = false
  LineAngle = 0
  LockPosition = false
  MeasureType = 1
  OverTolerance = 0
  References2D = -> [ProjItem]
  Rotation = 0
  ScaleType = 0
  TheoreticalExact = false
  Type = 2
  UnderTolerance = 0
  X = -65.7891
  Y = 30.0196
FEATURE [TechDraw::DrawViewDimension] Dimension011
  AngleOverride = false
  Arbitrary = false
  ArbitraryTolerances = false
  EqualTolerance = true
  ExtensionAngle = 0
  FormatSpec = %.2w
  FormatSpecOverTolerance = %+.2w
  FormatSpecUnderTolerance = %+.2w
  Inverted = false
  LineAngle = 0
  LockPosition = false
  MeasureType = 1
  OverTolerance = 0
  References2D = -> [SectionView]
  Rotation = 0
  ScaleType = 0
  TheoreticalExact = false
  Type = 1
  UnderTolerance = 0
  X = 7.50034
  Y = -8.08305
FEATURE [TechDraw::DrawViewDimension] Dimension012
  AngleOverride = false
  Arbitrary = false
  ArbitraryTolerances = false
  EqualTolerance = true
  ExtensionAngle = 0
  FormatSpec = %.2w
  FormatSpecOverTolerance = %+.2w
  FormatSpecUnderTolerance = %+.2w
  Inverted = false
  LineAngle = 0
  LockPosition = false
  MeasureType = 1
  OverTolerance = 0
  References2D = -> [SectionView]
  Rotation = 0
  ScaleType = 0
  TheoreticalExact = false
  Type = 1
  UnderTolerance = 0
  X = 15.8175
  Y = -53.6967
FEATURE [TechDraw::DrawViewDimension] Dimension013
  AngleOverride = false
  Arbitrary = false
  ArbitraryTolerances = false
  EqualTolerance = true
  ExtensionAngle = 0
  FormatSpec = %.2w
  FormatSpecOverTolerance = %+.2w
  FormatSpecUnderTolerance = %+.2w
  Inverted = false
  LineAngle = 0
  LockPosition = false
  MeasureType = 1
  OverTolerance = 0
  References2D = -> [SectionView]
  Rotation = 0
  ScaleType = 0
  TheoreticalExact = false
  Type = 2
  UnderTolerance = 0
  X = 13.592
  Y = 47.9705
FEATURE [TechDraw::DrawViewDimension] Dimension014
  AngleOverride = false
  Arbitrary = false
  ArbitraryTolerances = false
  EqualTolerance = true
  ExtensionAngle = 0
  FormatSpec = %.2w
  FormatSpecOverTolerance = %+.2w
  FormatSpecUnderTolerance = %+.2w
  Inverted = false
  LineAngle = 0
  LockPosition = false
  MeasureType = 1
  OverTolerance = 0
  References2D = -> [ProjItem002]
  Rotation = 0
  ScaleType = 0
  TheoreticalExact = false
  Type = 1
  UnderTolerance = 0
  X = -0.474718
  Y = 10.9185
FEATURE [TechDraw::DrawViewDimension] Dimension015
  AngleOverride = false
  Arbitrary = false
  ArbitraryTolerances = false
  EqualTolerance = true
  ExtensionAngle = 0
  FormatSpec = %.2w
  FormatSpecOverTolerance = %+.2w
  FormatSpecUnderTolerance = %+.2w
  Inverted = false
  LineAngle = 0
  LockPosition = false
  MeasureType = 1
  OverTolerance = 0
  References2D = -> [ProjItem002]
  Rotation = 0
  ScaleType = 0
  TheoreticalExact = false
  Type = 2
  UnderTolerance = 0
  X = -65.4543
  Y = 12.2317
FEATURE [TechDraw::DrawViewAnnotation] Annotation
  Font = osifont
  LineSpace = 80
  LockPosition = false
  MaxWidth = -1
  Rotation = 0
  ScaleType = 0
  Text = Ring with 8x 4.3mm through holes | (for M4 threaded rods passing | through). Ring is 5mm thick, | two beams crossing, beams are | 3mm thick and have 4x M3 threads
  TextSize = 5
  TextStyle = 0
  X = 241.195
  Y = 166.934
FEATURE [TechDraw::DrawPage] Page
  KeepUpdated = true
  NextBalloonIndex = 1
  ProjectionType = 0
  Template = -> Template
  Views = -> [ProjGroup,SectionView,Dimension,Dimension001,Dimension002,Dimension003,Dimension004,Dimension005,Dimension006,Dimension007,Dimension008,Dimension009,Dimension010,Dimension011,Dimension012,Dimension013,Dimension014,Dimension015,Annotation]
FEATURE [TechDraw::DrawSVGTemplate] Template001
  EditableTexts = Designed_by_Name=Thomas Spielauer; FC-Date=2023-11-15; FC-SC=mm; FC-SH=1/1; FC-Title=XL30 Attachment Base Ring; Subtitle=Base ring for stability
  Height = 210
  Orientation = 1
  Width = 297
FEATURE [TechDraw::DrawProjGroupItem] ProjItem003  label="Front001"
  CoarseView = false
  Direction = (0,0,1)
  Focus = 100
  HardHidden = false
  IsoCount = 0
  IsoHidden = false
  IsoVisible = false
  LockPosition = true
  Perspective = false
  Rotation = 0
  RotationVector = (1,0,0)
  ScaleType = 2
  SeamHidden = false
  SeamVisible = true
  SmoothHidden = false
  SmoothVisible = true
  Source = -> [Cut001]
  Type = 0
  X = 0
  XDirection = (1,0,0)
  Y = 0
FEATURE [TechDraw::DrawProjGroupItem] ProjItem004  label="Left"
  CoarseView = false
  Direction = (-1,0,1e-16)
  Focus = 100
  HardHidden = false
  IsoCount = 0
  IsoHidden = false
  IsoVisible = false
  LockPosition = false
  Perspective = false
  Rotation = 0
  RotationVector = (1,0,0)
  ScaleType = 2
  SeamHidden = false
  SeamVisible = true
  SmoothHidden = false
  SmoothVisible = true
  Source = -> [Cut001]
  Type = 1
  X = 87.2041
  XDirection = (1e-16,0,1)
  Y = 0
FEATURE [TechDraw::DrawProjGroup] ProjGroup001
  Anchor = -> ProjItem003
  AutoDistribute = true
  LockPosition = false
  ProjectionType = 0
  Rotation = 0
  ScaleType = 0
  Source = -> [Cut001]
  Views = -> [ProjItem003,ProjItem004]
  X = 98.0508
  Y = 130.02
  spacingX = 15
  spacingY = 15
FEATURE [TechDraw::DrawViewDimension] Dimension016
  AngleOverride = false
  Arbitrary = false
  ArbitraryTolerances = false
  EqualTolerance = true
  ExtensionAngle = 0
  FormatSpec = ⌀%.2w
  FormatSpecOverTolerance = %+.2w
  FormatSpecUnderTolerance = %+.2w
  Inverted = false
  LineAngle = 0
  LockPosition = false
  MeasureType = 1
  OverTolerance = 0
  References2D = -> [ProjItem003]
  Rotation = 0
  ScaleType = 0
  TheoreticalExact = false
  Type = 5
  UnderTolerance = 0
  X = 30.1616
  Y = 3.90021
FEATURE [TechDraw::DrawViewDimension] Dimension017
  AngleOverride = false
  Arbitrary = false
  ArbitraryTolerances = false
  EqualTolerance = true
  ExtensionAngle = 0
  FormatSpec = ⌀%.2w
  FormatSpecOverTolerance = %+.2w
  FormatSpecUnderTolerance = %+.2w
  Inverted = false
  LineAngle = 0
  LockPosition = false
  MeasureType = 1
  OverTolerance = 0
  References2D = -> [ProjItem003]
  Rotation = 0
  ScaleType = 0
  TheoreticalExact = false
  Type = 5
  UnderTolerance = 0
  X = 25.7414
  Y = 11.9606
FEATURE [TechDraw::DrawViewDimension] Dimension018
  AngleOverride = false
  Arbitrary = false
  ArbitraryTolerances = false
  EqualTolerance = true
  ExtensionAngle = 0
  FormatSpec = ⌀%.2w
  FormatSpecOverTolerance = %+.2w
  FormatSpecUnderTolerance = %+.2w
  Inverted = false
  LineAngle = 0
  LockPosition = false
  MeasureType = 1
  OverTolerance = 0
  References2D = -> [ProjItem003]
  Rotation = 0
  ScaleType = 0
  TheoreticalExact = false
  Type = 5
  UnderTolerance = 0
  X = -12.5673
  Y = 35.3185
FEATURE [TechDraw::DrawViewDimension] Dimension019
  AngleOverride = false
  Arbitrary = false
  ArbitraryTolerances = false
  EqualTolerance = true
  ExtensionAngle = 0
  FormatSpec = ⌀%.2w (8x)
  FormatSpecOverTolerance = %+.2w
  FormatSpecUnderTolerance = %+.2w
  Inverted = false
  LineAngle = 0
  LockPosition = false
  MeasureType = 1
  OverTolerance = 0
  References2D = -> [ProjItem003]
  Rotation = 0
  ScaleType = 0
  TheoreticalExact = false
  Type = 5
  UnderTolerance = 0
  X = 56.1196
  Y = 45.9358
FEATURE [TechDraw::DrawViewDimension] Dimension020
  AngleOverride = false
  Arbitrary = false
  ArbitraryTolerances = false
  EqualTolerance = true
  ExtensionAngle = 0
  FormatSpec = %.2w
  FormatSpecOverTolerance = %+.2w
  FormatSpecUnderTolerance = %+.2w
  Inverted = false
  LineAngle = 0
  LockPosition = false
  MeasureType = 1
  OverTolerance = 0
  References2D = -> [ProjItem004]
  Rotation = 0
  ScaleType = 0
  TheoreticalExact = false
  Type = 1
  UnderTolerance = 0
  X = 16.1
  Y = 67.274
FEATURE [TechDraw::DrawViewDimension] Dimension021
  AngleOverride = false
  Arbitrary = false
  ArbitraryTolerances = false
  EqualTolerance = true
  ExtensionAngle = 0
  FormatSpec = %.2w
  FormatSpecOverTolerance = %+.2w
  FormatSpecUnderTolerance = %+.2w
  Inverted = false
  LineAngle = 0
  LockPosition = false
  MeasureType = 1
  OverTolerance = 0
  References2D = -> [ProjItem004]
  Rotation = 0
  ScaleType = 0
  TheoreticalExact = false
  Type = 2
  UnderTolerance = 0
  X = -13.2256
  Y = 1.37674
FEATURE [TechDraw::DrawViewDimension] Dimension022
  AngleOverride = false
  Arbitrary = false
  ArbitraryTolerances = false
  EqualTolerance = true
  ExtensionAngle = 0
  FormatSpec = %.2w
  FormatSpecOverTolerance = %+.2w
  FormatSpecUnderTolerance = %+.2w
  Inverted = false
  LineAngle = 0
  LockPosition = false
  MeasureType = 1
  OverTolerance = 0
  References2D = -> [ProjItem003]
  Rotation = 0
  ScaleType = 0
  TheoreticalExact = false
  Type = 6
  UnderTolerance = 0
  X = -55.542
  Y = 41.3005
FEATURE [TechDraw::DrawPage] Page001
  KeepUpdated = true
  NextBalloonIndex = 1
  ProjectionType = 0
  Template = -> Template001
  Views = -> [ProjGroup001,Dimension016,Dimension017,Dimension018,Dimension019,Dimension020,Dimension021,Dimension022]
note: 2 file-system paths scrubbed to <path> (originals preserved in the JSON sidecar)
